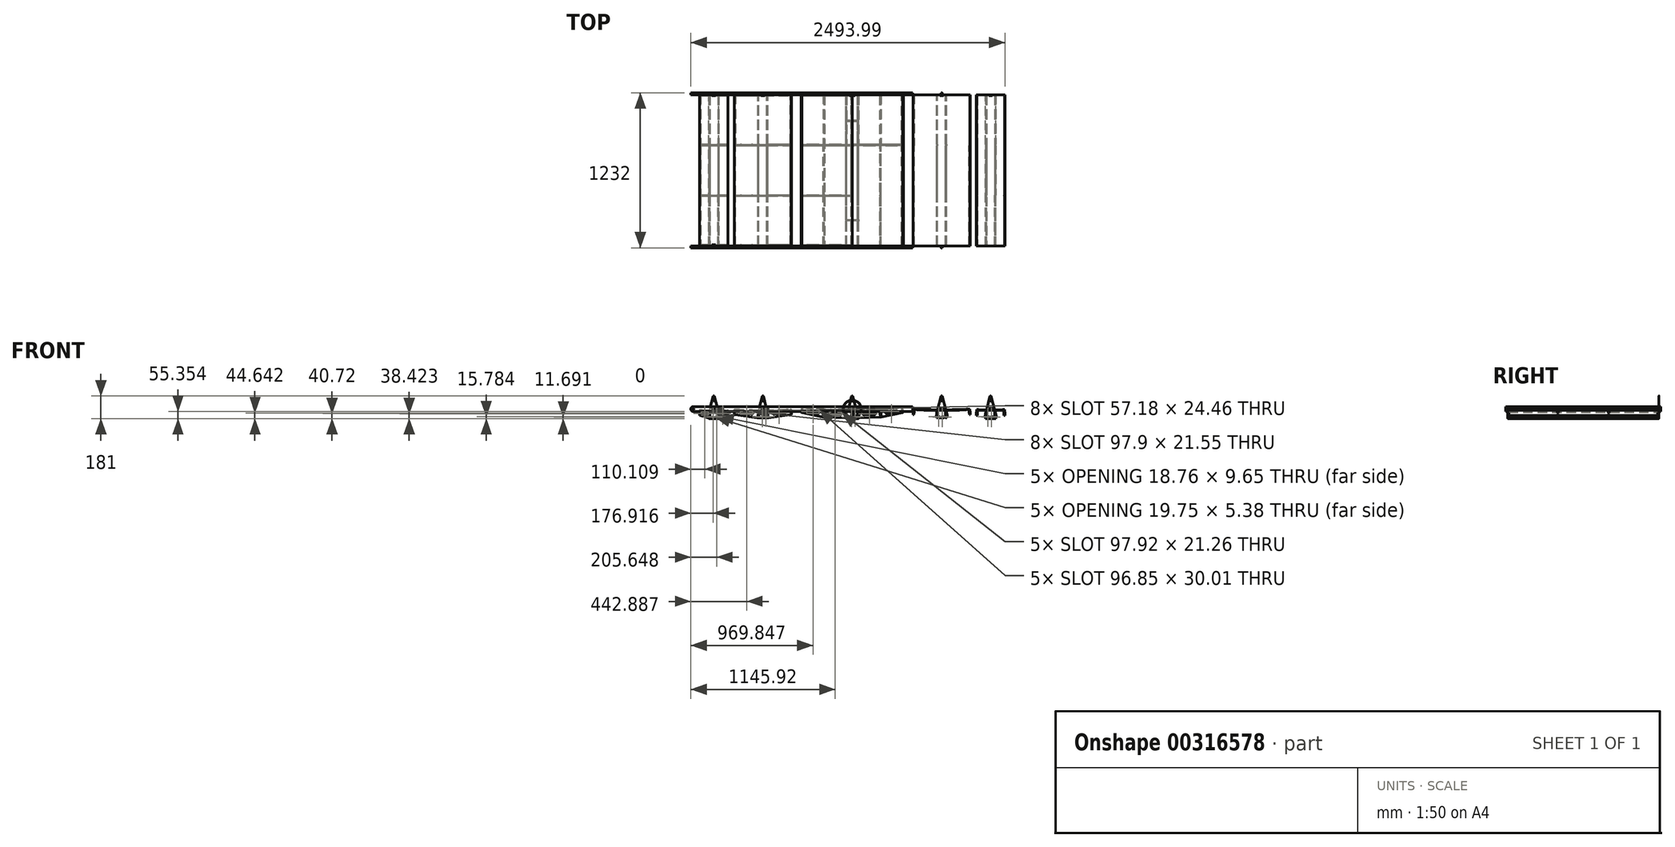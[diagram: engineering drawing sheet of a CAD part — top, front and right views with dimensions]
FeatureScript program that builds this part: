
annotation { "Feature Type Name" : "Feature", "Feature Type Description" : "" }
export const myFeature = defineFeature(function(context is Context, id is Id, definition is map)
    precondition{}
    {
        {
            assignVariable(context, id + "F0", {"name" : "ePlaque", "anyValue" : 8});
        }
        {
            assignVariable(context, id + "F1", {"name" : "lFacette", "anyValue" : 1200});
        }
        {
            var Q0;
            Q0=qCreatedBy(makeId("Front.planeOp"),FACE);
            var sketch = newSketch(context, id + "F2", { "sketchPlane" : qUnion([Q0])});
            skPoint(sketch, "E0", {"position": v(389.32, 0) * mm});
            skPoint(sketch, "E1", {"position": v(1098.97, 0) * mm});
            skPoint(sketch, "E2", {"position": v(1198.97, 1500) * mm});
            skCircle(sketch, "E3", {"center": v(0, 0) * mm, "radius": 112.5 * mm, "construction": true});
            skCircle(sketch, "E4", {"center": v(389.32, 0) * mm, "radius": 225 * mm, "construction": true});
            skCircle(sketch, "E5", {"center": v(1098.97, 0) * mm, "radius": 400 * mm, "construction": true});
            skLineSegment(sketch, "E6", {"start": v(112.5, 0) * mm, "end": v(164.32, 0) * mm, "construction": true});
            skLineSegment(sketch, "E7", {"start": v(614.32, 0) * mm, "end": v(698.97, 0) * mm, "construction": true});
            skLineSegment(sketch, "E8", {"start": v(1215.3, 382.71) * mm, "end": v(1098.97, 0) * mm, "construction": true});
            skLineSegment(sketch, "E9", {"start": v(716.26, 116.33) * mm, "end": v(1481.68, -116.33) * mm});
            skLineSegment(sketch, "E10", {"start": v(389.32, 0) * mm, "end": v(499.01, 196.45) * mm, "construction": true});
            skLineSegment(sketch, "E11", {"start": v(192.87, 109.7) * mm, "end": v(585.76, -109.7) * mm});
            skLineSegment(sketch, "E12", {"start": v(1098.97, 0) * mm, "end": v(1198.97, 1500) * mm, "construction": true});
            skLineSegment(sketch, "E13", {"start": v(389.32, 0) * mm, "end": v(1198.97, 1500) * mm, "construction": true});
            skLineSegment(sketch, "E14", {"start": v(0, 0) * mm, "end": v(1198.97, 1500) * mm, "construction": true});
            skLineSegment(sketch, "E15", {"start": v(389.32, 0) * mm, "end": v(501.82, 194.86) * mm, "construction": true});
            skLineSegment(sketch, "E16", {"start": v(0, 0) * mm, "end": v(56.25, 97.43) * mm, "construction": true});
            skLineSegment(sketch, "E17", {"start": v(1098.97, 0) * mm, "end": v(1298.97, 346.41) * mm, "construction": true});
            skLineSegment(sketch, "E18", {"start": v(-92.92, 63.43) * mm, "end": v(92.92, -63.43) * mm});
            skLineSegment(sketch, "E19", {"start": v(0, 0) * mm, "end": v(63.43, 92.92) * mm, "construction": true});
            skLineSegment(sketch, "E20", {"start": v(585.76, -109.7) * mm, "end": v(716.26, 116.33) * mm, "construction": true});
            skLineSegment(sketch, "E21", {"start": v(92.92, -63.43) * mm, "end": v(192.87, 109.7) * mm, "construction": true});
            skLineSegment(sketch, "E22", {"start": v(1198.97, 1500) * mm, "end": v(-92.92, 63.43) * mm, "construction": true});
            skSolve(sketch);
        }
        {
            var Q0;
            Q0=qCreatedBy(makeId("Front.planeOp"),FACE);
            var sketch = newSketch(context, id + "F3", { "sketchPlane" : qUnion([Q0])});
            skPoint(sketch, "E23", {"position": v(387.5, 0) * mm});
            skPoint(sketch, "E24", {"position": v(1082.5, 0) * mm});
            skPoint(sketch, "E25", {"position": v(1198.97, 1500) * mm});
            skCircle(sketch, "E26", {"center": v(0, 0) * mm, "radius": 112.5 * mm, "construction": true});
            skCircle(sketch, "E27", {"center": v(387.5, 0) * mm, "radius": 225 * mm, "construction": true});
            skCircle(sketch, "E28", {"center": v(1082.5, 0) * mm, "radius": 400 * mm, "construction": true});
            skLineSegment(sketch, "E29", {"start": v(112.5, 0) * mm, "end": v(162.5, 0) * mm, "construction": true});
            skLineSegment(sketch, "E30", {"start": v(612.5, 0) * mm, "end": v(682.5, 0) * mm, "construction": true});
            skLineSegment(sketch, "E31", {"start": v(1123.97, 1500) * mm, "end": v(1273.97, 1500) * mm});
            skLineSegment(sketch, "E32", {"start": v(1123.97, 1500) * mm, "end": v(1082.5, 0) * mm, "construction": true});
            skLineSegment(sketch, "E33", {"start": v(1273.97, 1500) * mm, "end": v(1082.5, 0) * mm, "construction": true});
            skLineSegment(sketch, "E34", {"start": v(1198.68, 1500) * mm, "end": v(1082.5, 0) * mm, "construction": true});
            skLineSegment(sketch, "E35", {"start": v(683.7, 30.89) * mm, "end": v(1481.3, -30.89) * mm});
            skLineSegment(sketch, "E36", {"start": v(1123.97, 1500) * mm, "end": v(683.7, 30.89) * mm, "construction": true});
            skLineSegment(sketch, "E37", {"start": v(1481.3, -30.89) * mm, "end": v(1273.97, 1500) * mm, "construction": true});
            skLineSegment(sketch, "E38", {"start": v(1210.93, 1636.1) * mm, "end": v(1481.3, -30.89) * mm, "construction": true});
            skLineSegment(sketch, "E39", {"start": v(683.7, 30.89) * mm, "end": v(1210.93, 1636.1) * mm, "construction": true});
            skLineSegment(sketch, "E40", {"start": v(1082.5, 0) * mm, "end": v(1210.93, 1636.1) * mm, "construction": true});
            skLineSegment(sketch, "E41", {"start": v(1210.93, 1636.1) * mm, "end": v(1337.66, 3272.32) * mm, "construction": true});
            skSolve(sketch);
        }
        {
            var Q0;
            Q0=qCreatedBy(makeId("Front.planeOp"),FACE);
            var sketch = newSketch(context, id + "F4", { "sketchPlane" : qUnion([Q0])});
            skCircle(sketch, "E42.0", {"center": v(387.5, 0) * mm, "radius": 225 * mm, "construction": true});
            skPoint(sketch, "E42.1", {"position": v(387.5, 0) * mm});
            skLineSegment(sketch, "E42.2", {"start": v(1123.97, 1500) * mm, "end": v(1273.97, 1500) * mm});
            skLineSegment(sketch, "E43", {"start": v(1123.97, 1500) * mm, "end": v(387.5, 0) * mm, "construction": true});
            skLineSegment(sketch, "E44", {"start": v(387.5, 0) * mm, "end": v(1273.97, 1500) * mm, "construction": true});
            skLineSegment(sketch, "E45", {"start": v(387.5, 0) * mm, "end": v(1197.4, 1500) * mm, "construction": true});
            skLineSegment(sketch, "E46", {"start": v(189.52, 106.9) * mm, "end": v(585.48, -106.9) * mm});
            skLineSegment(sketch, "E47", {"start": v(189.52, 106.9) * mm, "end": v(1123.97, 1500) * mm, "construction": true});
            skLineSegment(sketch, "E48", {"start": v(585.48, -106.9) * mm, "end": v(1273.97, 1500) * mm, "construction": true});
            skLineSegment(sketch, "E49", {"start": v(189.52, 106.9) * mm, "end": v(1284.6, 1650.54) * mm, "construction": true});
            skLineSegment(sketch, "E50", {"start": v(1284.6, 1650.54) * mm, "end": v(585.48, -106.9) * mm, "construction": true});
            skLineSegment(sketch, "E51", {"start": v(387.5, 0) * mm, "end": v(1284.6, 1650.54) * mm, "construction": true});
            skLineSegment(sketch, "E52", {"start": v(1284.6, 1650.54) * mm, "end": v(2181.71, 3301.09) * mm, "construction": true});
            skSolve(sketch);
        }
        {
            var Q0;
            Q0=qCreatedBy(makeId("Front.planeOp"),FACE);
            var sketch = newSketch(context, id + "F5", { "sketchPlane" : qUnion([Q0])});
            skLineSegment(sketch, "E53.0", {"start": v(1123.97, 1500) * mm, "end": v(1273.97, 1500) * mm});
            skCircle(sketch, "E54.0", {"center": v(0, 0) * mm, "radius": 112.5 * mm, "construction": true});
            skLineSegment(sketch, "E55", {"start": v(1123.97, 1500) * mm, "end": v(0, 0) * mm, "construction": true});
            skLineSegment(sketch, "E56", {"start": v(0, 0) * mm, "end": v(1273.97, 1500) * mm, "construction": true});
            skLineSegment(sketch, "E57", {"start": v(0, 0) * mm, "end": v(1197.14, 1500) * mm, "construction": true});
            skLineSegment(sketch, "E58", {"start": v(-87.93, 70.18) * mm, "end": v(87.93, -70.18) * mm});
            skLineSegment(sketch, "E59", {"start": v(-87.93, 70.18) * mm, "end": v(1123.97, 1500) * mm, "construction": true});
            skLineSegment(sketch, "E60", {"start": v(1273.97, 1500) * mm, "end": v(87.93, -70.18) * mm, "construction": true});
            skLineSegment(sketch, "E61", {"start": v(87.93, -70.18) * mm, "end": v(1294.24, 1616.9) * mm, "construction": true});
            skLineSegment(sketch, "E62", {"start": v(-87.93, 70.18) * mm, "end": v(1294.24, 1616.9) * mm, "construction": true});
            skLineSegment(sketch, "E63", {"start": v(1294.24, 1616.9) * mm, "end": v(0, 0) * mm, "construction": true});
            skLineSegment(sketch, "E64", {"start": v(1294.24, 1616.9) * mm, "end": v(2588.47, 3233.81) * mm, "construction": true});
            skSolve(sketch);
        }
        {
            var Q0;
            Q0=qCreatedBy(makeId("Front.planeOp"),FACE);
            var sketch = newSketch(context, id + "F6", { "sketchPlane" : qUnion([Q0])});
            skCircle(sketch, "E65.0", {"center": v(1098.97, 0) * mm, "radius": 400 * mm, "construction": true});
            skLineSegment(sketch, "E66.3", {"start": v(1123.97, 1500) * mm, "end": v(1273.97, 1500) * mm});
            skLineSegment(sketch, "E67", {"start": v(1337.66, 3272.32) * mm, "end": v(1098.97, 0) * mm, "construction": true});
            skLineSegment(sketch, "E68", {"start": v(751.34, -197.87) * mm, "end": v(1446.6, 197.87) * mm});
            skLineSegment(sketch, "E69", {"start": v(1446.6, 197.87) * mm, "end": v(-511.93, 2830.2) * mm, "construction": true});
            skLineSegment(sketch, "E70", {"start": v(-511.93, 2830.2) * mm, "end": v(751.34, -197.87) * mm, "construction": true});
            skLineSegment(sketch, "E71", {"start": v(52.02, 190.67) * mm, "end": v(751.34, -197.87) * mm, "construction": true});
            skLineSegment(sketch, "E72", {"start": v(747.3, 586.4) * mm, "end": v(1446.6, 197.87) * mm, "construction": true});
            skLineSegment(sketch, "E73", {"start": v(751.34, -197.87) * mm, "end": v(1190.2, 1368.3) * mm, "construction": true});
            skLineSegment(sketch, "E74", {"start": v(1190.2, 1368.3) * mm, "end": v(1446.6, 197.87) * mm, "construction": true});
            skLineSegment(sketch, "E75", {"start": v(751.34, -197.87) * mm, "end": v(1275.4, 1500) * mm, "construction": true});
            skLineSegment(sketch, "E76", {"start": v(1446.6, 197.87) * mm, "end": v(1125.4, 1500) * mm, "construction": true});
            skLineSegment(sketch, "E77", {"start": v(1125.4, 1500) * mm, "end": v(1275.4, 1500) * mm, "construction": true});
            skLineSegment(sketch, "E78", {"start": v(1198.97, 1500) * mm, "end": v(1098.97, 0) * mm, "construction": true});
            skPoint(sketch, "E79.0", {"position": v(1337.66, 3272.32) * mm});
            skSolve(sketch);
        }
        {
            var Q0;
            Q0=qCreatedBy(makeId("Front.planeOp"),FACE);
            var sketch = newSketch(context, id + "F7", { "sketchPlane" : qUnion([Q0])});
            skLineSegment(sketch, "E80", {"start": v(389.32, 0) * mm, "end": v(2181.71, 3301.09) * mm, "construction": true});
            skLineSegment(sketch, "E81", {"start": v(166.24, -29.34) * mm, "end": v(612.4, 29.34) * mm});
            skLineSegment(sketch, "E82", {"start": v(166.24, -29.34) * mm, "end": v(-99.65, 3717.55) * mm, "construction": true});
            skLineSegment(sketch, "E83", {"start": v(-99.65, 3717.55) * mm, "end": v(612.4, 29.34) * mm, "construction": true});
            skLineSegment(sketch, "E84", {"start": v(-137.98, 302.25) * mm, "end": v(166.24, -29.34) * mm, "construction": true});
            skLineSegment(sketch, "E85", {"start": v(308.18, 360.93) * mm, "end": v(612.4, 29.34) * mm, "construction": true});
            skLineSegment(sketch, "E86", {"start": v(166.24, -29.34) * mm, "end": v(1110.47, 1348.82) * mm, "construction": true});
            skLineSegment(sketch, "E87", {"start": v(1110.47, 1348.82) * mm, "end": v(612.4, 29.34) * mm, "construction": true});
            skCircle(sketch, "E88.0", {"center": v(389.32, 0) * mm, "radius": 225 * mm, "construction": true});
            skLineSegment(sketch, "E89.0", {"start": v(1123.97, 1500) * mm, "end": v(1273.97, 1500) * mm});
            skLineSegment(sketch, "E90", {"start": v(166.24, -29.34) * mm, "end": v(1273.97, 1500) * mm, "construction": true});
            skLineSegment(sketch, "E91", {"start": v(612.4, 29.34) * mm, "end": v(1123.97, 1500) * mm, "construction": true});
            skPoint(sketch, "E92.0", {"position": v(2181.71, 3301.09) * mm});
            skSolve(sketch);
        }
        {
            var Q0;
            Q0=qCreatedBy(makeId("Front.planeOp"),FACE);
            var sketch = newSketch(context, id + "F8", { "sketchPlane" : qUnion([Q0])});
            skLineSegment(sketch, "E93", {"start": v(0, 0) * mm, "end": v(2588.47, 3233.81) * mm, "construction": true});
            skLineSegment(sketch, "E94", {"start": v(-111.64, 13.9) * mm, "end": v(111.64, -13.9) * mm});
            skLineSegment(sketch, "E95", {"start": v(-111.64, 13.9) * mm, "end": v(511.32, 4108.97) * mm, "construction": true});
            skLineSegment(sketch, "E96", {"start": v(-203.86, 219.13) * mm, "end": v(-111.64, 13.9) * mm, "construction": true});
            skLineSegment(sketch, "E97", {"start": v(511.32, 4108.97) * mm, "end": v(111.64, -13.9) * mm, "construction": true});
            skLineSegment(sketch, "E98", {"start": v(19.42, 191.34) * mm, "end": v(111.64, -13.9) * mm, "construction": true});
            skLineSegment(sketch, "E99", {"start": v(111.64, -13.9) * mm, "end": v(1100.2, 1383.84) * mm, "construction": true});
            skLineSegment(sketch, "E100", {"start": v(-111.64, 13.9) * mm, "end": v(1100.2, 1383.84) * mm, "construction": true});
            skLineSegment(sketch, "E101.0", {"start": v(1123.97, 1500) * mm, "end": v(1273.97, 1500) * mm});
            skCircle(sketch, "E102.0", {"center": v(0, 0) * mm, "radius": 112.5 * mm, "construction": true});
            skPoint(sketch, "E103.0", {"position": v(2588.47, 3233.81) * mm});
            skLineSegment(sketch, "E104", {"start": v(111.64, -13.9) * mm, "end": v(1123.97, 1500) * mm, "construction": true});
            skLineSegment(sketch, "E105", {"start": v(-111.64, 13.9) * mm, "end": v(1273.97, 1500) * mm, "construction": true});
            skSolve(sketch);
        }
        {
            var Q0;
            Q0=qCreatedBy(makeId("Front.planeOp"),FACE);
            var sketch = newSketch(context, id + "F9", { "sketchPlane" : qUnion([Q0])});
            skArc(sketch, "E106", {"start": v(-112.5, -9.47) * mm, "mid": v(0, -11) * mm, "end": v(112.5, -9.47) * mm});
            skLineSegment(sketch, "E107", {"start": v(-13.5, -5.98) * mm, "end": v(-13.5, 6) * mm});
            skLineSegment(sketch, "E108", {"start": v(-13.5, 6) * mm, "end": v(13.5, 6) * mm});
            skLineSegment(sketch, "E109", {"start": v(13.5, 6) * mm, "end": v(13.5, 0.5) * mm});
            skLineSegment(sketch, "E110", {"start": v(0, 0) * mm, "end": v(0, -6) * mm, "construction": true});
            skArc(sketch, "E111", {"start": v(4.47, 0.5) * mm, "mid": v(-4.5, 0) * mm, "end": v(4.47, -0.5) * mm});
            skLineSegment(sketch, "E112", {"start": v(-35.49, -10.85) * mm, "end": v(-36, -70.85) * mm, "construction": true});
            skLineSegment(sketch, "E113", {"start": v(-40, -70.81) * mm, "end": v(-32, -70.88) * mm});
            skLineSegment(sketch, "E114", {"start": v(-40, -70.81) * mm, "end": v(-39.49, -10.81) * mm});
            skLineSegment(sketch, "E115", {"start": v(-32, -70.88) * mm, "end": v(-31.49, -10.88) * mm});
            skLineSegment(sketch, "E116", {"start": v(-108.5, -9.58) * mm, "end": v(-109.55, -49.57) * mm, "construction": true});
            skLineSegment(sketch, "E117", {"start": v(-112.5, -9.47) * mm, "end": v(-113.55, -49.46) * mm});
            skLineSegment(sketch, "E118", {"start": v(-113.55, -49.46) * mm, "end": v(-105.55, -49.67) * mm});
            skLineSegment(sketch, "E119", {"start": v(-105.55, -49.67) * mm, "end": v(-104.5, -9.68) * mm});
            skArc(sketch, "E120", {"start": v(-112.36, -4.48) * mm, "mid": v(0, -6) * mm, "end": v(112.36, -4.48) * mm});
            skLineSegment(sketch, "E121", {"start": v(-112.36, -4.48) * mm, "end": v(-112.5, -9.47) * mm});
            skLineSegment(sketch, "E122", {"start": v(112.5, -9.47) * mm, "end": v(112.36, -4.48) * mm});
            skLineSegment(sketch, "E123.MirrorCS", {"start": v(113.55, -49.46) * mm, "end": v(105.55, -49.67) * mm});
            skLineSegment(sketch, "E124.MirrorCS", {"start": v(112.5, -9.47) * mm, "end": v(113.55, -49.46) * mm});
            skLineSegment(sketch, "E125.MirrorCS", {"start": v(105.55, -49.67) * mm, "end": v(104.5, -9.68) * mm});
            skLineSegment(sketch, "E126.MirrorCS", {"start": v(40, -70.81) * mm, "end": v(39.49, -10.81) * mm});
            skLineSegment(sketch, "E127.MirrorCS", {"start": v(32, -70.88) * mm, "end": v(31.49, -10.88) * mm});
            skLineSegment(sketch, "E128.MirrorCS", {"start": v(40, -70.81) * mm, "end": v(32, -70.88) * mm});
            skLineSegment(sketch, "E129.bottom", {"start": v(-40, -70.81) * mm, "end": v(40, -70.81) * mm, "construction": true});
            skLineSegment(sketch, "E129.left", {"start": v(-40, -70.81) * mm, "end": v(-40, -75.81) * mm});
            skLineSegment(sketch, "E129.right", {"start": v(40, -70.81) * mm, "end": v(40, -75.81) * mm});
            skLineSegment(sketch, "E130", {"start": v(-105.55, -49.67) * mm, "end": v(-40, -70.81) * mm});
            skLineSegment(sketch, "E131", {"start": v(-113.02, -29.47) * mm, "end": v(-105.03, -29.68) * mm});
            skLineSegment(sketch, "E132", {"start": v(-39.74, -40.81) * mm, "end": v(-31.74, -40.88) * mm});
            skLineSegment(sketch, "E133.MirrorCS", {"start": v(113.02, -29.47) * mm, "end": v(105.03, -29.68) * mm});
            skLineSegment(sketch, "E134.MirrorCS", {"start": v(105.55, -49.67) * mm, "end": v(40, -70.81) * mm});
            skLineSegment(sketch, "E135.MirrorCS", {"start": v(39.74, -40.81) * mm, "end": v(31.74, -40.88) * mm});
            skArc(sketch, "E136", {"start": v(393.79, 0.5) * mm, "mid": v(384.82, 0) * mm, "end": v(393.79, -0.5) * mm});
            skLineSegment(sketch, "E137", {"start": v(389.32, 0) * mm, "end": v(389.32, -6) * mm, "construction": true});
            skArc(sketch, "E138", {"start": v(164.32, 0.74) * mm, "mid": v(389.32, -6) * mm, "end": v(614.32, 0.74) * mm});
            skArc(sketch, "E139", {"start": v(164.02, -4.25) * mm, "mid": v(389.32, -11) * mm, "end": v(614.62, -4.25) * mm});
            skLineSegment(sketch, "E140", {"start": v(164.32, 0.74) * mm, "end": v(164.02, -4.25) * mm});
            skLineSegment(sketch, "E141", {"start": v(353.32, -70.83) * mm, "end": v(353.88, -10.83) * mm, "construction": true});
            skLineSegment(sketch, "E142", {"start": v(165.66, -44.41) * mm, "end": v(168, -4.48) * mm, "construction": true});
            skLineSegment(sketch, "E143", {"start": v(164.02, -4.25) * mm, "end": v(161.66, -44.18) * mm});
            skLineSegment(sketch, "E144", {"start": v(161.66, -44.18) * mm, "end": v(169.65, -44.65) * mm});
            skLineSegment(sketch, "E145", {"start": v(169.65, -44.65) * mm, "end": v(172, -4.72) * mm});
            skLineSegment(sketch, "E146", {"start": v(349.88, -10.8) * mm, "end": v(349.32, -70.8) * mm});
            skLineSegment(sketch, "E147", {"start": v(349.32, -70.8) * mm, "end": v(357.32, -70.87) * mm});
            skLineSegment(sketch, "E148", {"start": v(357.32, -70.87) * mm, "end": v(357.88, -10.87) * mm});
            skLineSegment(sketch, "E149.MirrorCS", {"start": v(421.32, -70.87) * mm, "end": v(420.75, -10.87) * mm});
            skLineSegment(sketch, "E150.MirrorCS", {"start": v(428.75, -10.8) * mm, "end": v(429.32, -70.8) * mm});
            skLineSegment(sketch, "E151.MirrorCS", {"start": v(429.32, -70.8) * mm, "end": v(421.32, -70.87) * mm});
            skLineSegment(sketch, "E152.MirrorCS", {"start": v(614.62, -4.25) * mm, "end": v(616.97, -44.18) * mm});
            skLineSegment(sketch, "E153.MirrorCS", {"start": v(616.97, -44.18) * mm, "end": v(608.98, -44.65) * mm});
            skLineSegment(sketch, "E154.MirrorCS", {"start": v(608.98, -44.65) * mm, "end": v(606.63, -4.72) * mm});
            skLineSegment(sketch, "E155.bottom", {"start": v(349.32, -70.8) * mm, "end": v(429.32, -70.8) * mm, "construction": true});
            skLineSegment(sketch, "E156", {"start": v(169.65, -44.65) * mm, "end": v(349.32, -70.8) * mm});
            skLineSegment(sketch, "E157", {"start": v(162.84, -24.21) * mm, "end": v(170.83, -24.68) * mm});
            skLineSegment(sketch, "E158", {"start": v(349.6, -40.8) * mm, "end": v(357.6, -40.87) * mm});
            skLineSegment(sketch, "E159.MirrorCS", {"start": v(429.03, -40.8) * mm, "end": v(421.03, -40.87) * mm});
            skLineSegment(sketch, "E160.MirrorCS", {"start": v(608.98, -44.65) * mm, "end": v(429.32, -70.8) * mm});
            skLineSegment(sketch, "E161.MirrorCS", {"start": v(615.8, -24.21) * mm, "end": v(607.8, -24.68) * mm});
            skLineSegment(sketch, "E162.MirrorCS", {"start": v(614.32, 0.74) * mm, "end": v(614.62, -4.25) * mm});
            skLineSegment(sketch, "E163", {"start": v(375.82, -5.98) * mm, "end": v(375.82, 6) * mm});
            skLineSegment(sketch, "E164", {"start": v(375.82, 6) * mm, "end": v(402.82, 6) * mm});
            skLineSegment(sketch, "E165", {"start": v(402.82, 6) * mm, "end": v(402.82, 0.5) * mm});
            skLineSegment(sketch, "E166", {"start": v(0, 0) * mm, "end": v(13.5, 0) * mm, "construction": true});
            skLineSegment(sketch, "E167", {"start": v(13.5, 0.5) * mm, "end": v(4.47, 0.5) * mm});
            skLineSegment(sketch, "E168", {"start": v(13.5, -0.5) * mm, "end": v(4.47, -0.5) * mm});
            skLineSegment(sketch, "E169.trimOffspring", {"start": v(13.5, -0.5) * mm, "end": v(13.5, -5.98) * mm});
            skLineSegment(sketch, "E170", {"start": v(13.5, 0.5) * mm, "end": v(13.5, -0.5) * mm, "construction": true});
            skLineSegment(sketch, "E171", {"start": v(402.82, 0.5) * mm, "end": v(393.79, 0.5) * mm});
            skLineSegment(sketch, "E172", {"start": v(402.82, -0.5) * mm, "end": v(393.79, -0.5) * mm});
            skLineSegment(sketch, "E173.trimOffspring", {"start": v(402.82, -0.5) * mm, "end": v(402.82, -5.98) * mm});
            skPoint(sketch, "E174", {"position": v(1098.97, 0) * mm});
            skCircle(sketch, "E175", {"center": v(1098.97, 0) * mm, "radius": 4.5 * mm});
            skArc(sketch, "E176", {"start": v(698.97, 18.45) * mm, "mid": v(1098.97, -6) * mm, "end": v(1498.97, 18.45) * mm});
            skLineSegment(sketch, "E177", {"start": v(1098.97, 0) * mm, "end": v(1098.97, -6) * mm, "construction": true});
            skLineSegment(sketch, "E178", {"start": v(698.97, 18.45) * mm, "end": v(698.36, 13.49) * mm});
            skLineSegment(sketch, "E179.MirrorCS", {"start": v(1498.97, 18.45) * mm, "end": v(1499.58, 13.49) * mm});
            skArc(sketch, "E180", {"start": v(698.36, 13.49) * mm, "mid": v(1098.97, -11) * mm, "end": v(1499.58, 13.49) * mm});
            skLineSegment(sketch, "E181", {"start": v(702.33, 13) * mm, "end": v(697.5, -26.7) * mm, "construction": true});
            skLineSegment(sketch, "E182", {"start": v(706.3, 12.52) * mm, "end": v(701.48, -27.19) * mm});
            skLineSegment(sketch, "E183", {"start": v(701.48, -27.19) * mm, "end": v(693.54, -26.22) * mm});
            skLineSegment(sketch, "E184", {"start": v(693.54, -26.22) * mm, "end": v(698.36, 13.49) * mm});
            skLineSegment(sketch, "E185", {"start": v(695.95, -6.37) * mm, "end": v(703.9, -7.33) * mm});
            skLineSegment(sketch, "E186.MirrorCS", {"start": v(1496.46, -27.19) * mm, "end": v(1504.4, -26.22) * mm});
            skLineSegment(sketch, "E187.MirrorCS", {"start": v(1504.4, -26.22) * mm, "end": v(1499.58, 13.49) * mm});
            skLineSegment(sketch, "E188.MirrorCS", {"start": v(1491.64, 12.52) * mm, "end": v(1496.46, -27.19) * mm});
            skLineSegment(sketch, "E189.MirrorCS", {"start": v(1502, -6.37) * mm, "end": v(1494.05, -7.33) * mm});
            skLineSegment(sketch, "E190", {"start": v(876.94, -3.5) * mm, "end": v(872.9, -63.36) * mm, "construction": true});
            skLineSegment(sketch, "E191", {"start": v(872.95, -3.23) * mm, "end": v(868.9, -63.1) * mm});
            skLineSegment(sketch, "E192", {"start": v(868.9, -63.1) * mm, "end": v(876.88, -63.63) * mm});
            skLineSegment(sketch, "E193", {"start": v(876.88, -63.63) * mm, "end": v(880.93, -3.77) * mm});
            skLineSegment(sketch, "E194", {"start": v(870.93, -33.16) * mm, "end": v(878.9, -33.7) * mm});
            skLineSegment(sketch, "E195", {"start": v(701.48, -27.19) * mm, "end": v(868.9, -63.1) * mm});
            skLineSegment(sketch, "E196", {"start": v(1098.97, -11) * mm, "end": v(1098.97, -51) * mm});
            skLineSegment(sketch, "E197", {"start": v(1090.97, -11) * mm, "end": v(1090.97, -51) * mm});
            skLineSegment(sketch, "E198", {"start": v(1090.97, -51) * mm, "end": v(1106.97, -51) * mm});
            skLineSegment(sketch, "E199", {"start": v(1106.97, -51) * mm, "end": v(1106.97, -11) * mm});
            skLineSegment(sketch, "E200", {"start": v(1090.97, -31) * mm, "end": v(1098.97, -31) * mm});
            skLineSegment(sketch, "E201", {"start": v(1098.97, -31) * mm, "end": v(1106.97, -31) * mm});
            skLineSegment(sketch, "E202.bottom", {"start": v(1047.97, -75.66) * mm, "end": v(1149.97, -75.66) * mm});
            skLineSegment(sketch, "E202.top", {"start": v(1047.97, -70.66) * mm, "end": v(1149.97, -70.66) * mm});
            skLineSegment(sketch, "E202.left", {"start": v(1047.97, -75.66) * mm, "end": v(1047.97, -70.66) * mm});
            skLineSegment(sketch, "E202.right", {"start": v(1149.97, -75.66) * mm, "end": v(1149.97, -70.66) * mm});
            skLineSegment(sketch, "E203", {"start": v(1047.97, -70.66) * mm, "end": v(1047.97, -10.66) * mm});
            skLineSegment(sketch, "E204", {"start": v(1047.97, -10.66) * mm, "end": v(1055.97, -10.66) * mm});
            skLineSegment(sketch, "E205", {"start": v(1055.97, -10.66) * mm, "end": v(1055.97, -70.66) * mm});
            skLineSegment(sketch, "E206", {"start": v(1047.97, -40.66) * mm, "end": v(1055.97, -40.66) * mm});
            skLineSegment(sketch, "E207.MirrorCS", {"start": v(1149.97, -70.66) * mm, "end": v(1149.97, -10.66) * mm});
            skLineSegment(sketch, "E208.MirrorCS", {"start": v(1149.97, -10.66) * mm, "end": v(1141.97, -10.66) * mm});
            skLineSegment(sketch, "E209.MirrorCS", {"start": v(1141.97, -10.66) * mm, "end": v(1141.97, -70.66) * mm});
            skLineSegment(sketch, "E210.MirrorCS", {"start": v(1149.97, -40.66) * mm, "end": v(1141.97, -40.66) * mm});
            skLineSegment(sketch, "E211", {"start": v(876.88, -63.63) * mm, "end": v(1047.97, -70.66) * mm});
            skLineSegment(sketch, "E212.MirrorCS", {"start": v(1496.46, -27.19) * mm, "end": v(1329.04, -63.1) * mm});
            skLineSegment(sketch, "E213.MirrorCS", {"start": v(1321.06, -63.63) * mm, "end": v(1149.97, -70.66) * mm});
            skLineSegment(sketch, "E214.MirrorCS", {"start": v(1329.04, -63.1) * mm, "end": v(1321.06, -63.63) * mm});
            skLineSegment(sketch, "E215.MirrorCS", {"start": v(1324.99, -3.23) * mm, "end": v(1329.04, -63.1) * mm});
            skLineSegment(sketch, "E216.MirrorCS", {"start": v(1321.06, -63.63) * mm, "end": v(1317, -3.77) * mm});
            skLineSegment(sketch, "E217.MirrorCS", {"start": v(1327.01, -33.16) * mm, "end": v(1319.03, -33.7) * mm});
            skLineSegment(sketch, "E218", {"start": v(1098.97, -6) * mm, "end": v(1098.97, -11) * mm});
            skLineSegment(sketch, "E219", {"start": v(1051.97, -10.66) * mm, "end": v(1051.97, -40.66) * mm, "construction": true});
            skArc(sketch, "E220", {"start": v(-40, -70.81) * mm, "mid": v(0, -71) * mm, "end": v(40, -70.81) * mm});
            skArc(sketch, "E221", {"start": v(-40, -75.81) * mm, "mid": v(0, -76) * mm, "end": v(40, -75.81) * mm});
            skArc(sketch, "E222", {"start": v(349.32, -70.8) * mm, "mid": v(389.32, -71) * mm, "end": v(429.32, -70.8) * mm});
            skLineSegment(sketch, "E223", {"start": v(1047.97, -73.16) * mm, "end": v(1098.97, -73.16) * mm, "construction": true});
            skLineSegment(sketch, "E224", {"start": v(1098.97, 0) * mm, "end": v(1098.97, -51) * mm, "construction": true});
            skLineSegment(sketch, "E225", {"start": v(1098.97, -51) * mm, "end": v(1098.97, -70.66) * mm});
            skLineSegment(sketch, "E226", {"start": v(1090.97, -51) * mm, "end": v(1083.97, -51) * mm});
            skLineSegment(sketch, "E227", {"start": v(1083.97, -51) * mm, "end": v(1083.97, -59) * mm});
            skLineSegment(sketch, "E228.MirrorCS", {"start": v(1106.97, -51) * mm, "end": v(1113.97, -51) * mm});
            skLineSegment(sketch, "E229.MirrorCS", {"start": v(1113.97, -51) * mm, "end": v(1113.97, -59) * mm});
            skLineSegment(sketch, "E230", {"start": v(1083.97, -59) * mm, "end": v(1113.97, -59) * mm});
            skLineSegment(sketch, "E231", {"start": v(1083.97, -55) * mm, "end": v(1098.97, -55) * mm, "construction": true});
            skLineSegment(sketch, "E232", {"start": v(1051.97, -70.66) * mm, "end": v(1051.97, -55.66) * mm, "construction": true});
            skLineSegment(sketch, "E233", {"start": v(1047.97, -63.16) * mm, "end": v(1055.97, -63.16) * mm});
            skLineSegment(sketch, "E234", {"start": v(1098.97, -63.16) * mm, "end": v(1051.97, -63.16) * mm, "construction": true});
            skLineSegment(sketch, "E235", {"start": v(1055.97, -55.66) * mm, "end": v(1141.97, -55) * mm});
            skLineSegment(sketch, "E236.MirrorCS", {"start": v(1149.97, -63.16) * mm, "end": v(1141.97, -63.16) * mm});
            skLineSegment(sketch, "E237", {"start": v(1076.44, -5.92) * mm, "end": v(1076.44, -0.5) * mm});
            skLineSegment(sketch, "E238", {"start": v(1076.44, -0.5) * mm, "end": v(1094.5, -0.5) * mm});
            skLineSegment(sketch, "E239.bottom", {"start": v(1085.47, 6) * mm, "end": v(1112.47, 6) * mm});
            skLineSegment(sketch, "E239.top", {"start": v(1085.47, 0.5) * mm, "end": v(1112.47, 0.5) * mm});
            skLineSegment(sketch, "E239.left", {"start": v(1085.47, 6) * mm, "end": v(1085.47, 0.5) * mm});
            skLineSegment(sketch, "E239.right", {"start": v(1112.47, 6) * mm, "end": v(1112.47, 0.5) * mm});
            skCircle(sketch, "E240", {"center": v(1098.97, 0) * mm, "radius": 6 * mm});
            skLineSegment(sketch, "E241.MirrorCS", {"start": v(1121.5, -0.5) * mm, "end": v(1103.44, -0.5) * mm});
            skLineSegment(sketch, "E242.MirrorCS", {"start": v(1121.5, -5.92) * mm, "end": v(1121.5, -0.5) * mm});
            skLineSegment(sketch, "E243", {"start": v(1085.47, 0.5) * mm, "end": v(1076.44, 0.5) * mm, "construction": true});
            skCircle(sketch, "E244", {"center": v(0, 0) * mm, "radius": 3 * mm});
            skPoint(sketch, "E245.0", {"position": v(1337.66, 3272.32) * mm});
            skPoint(sketch, "E246.0", {"position": v(2181.71, 3301.09) * mm});
            skPoint(sketch, "E247.0", {"position": v(2588.47, 3233.81) * mm});
            skLineSegment(sketch, "E248", {"start": v(1337.66, 3272.32) * mm, "end": v(1098.97, 0) * mm, "construction": true});
            skLineSegment(sketch, "E249", {"start": v(1098.97, -3) * mm, "end": v(1098.97, 3278.02) * mm, "construction": true});
            skLineSegment(sketch, "E250", {"start": v(389.32, 0) * mm, "end": v(2181.71, 3301.09) * mm, "construction": true});
            skLineSegment(sketch, "E251", {"start": v(389.32, -6) * mm, "end": v(389.32, 3750.31) * mm, "construction": true});
            skLineSegment(sketch, "E252", {"start": v(0, 0) * mm, "end": v(2588.47, 3233.81) * mm, "construction": true});
            skLineSegment(sketch, "E253", {"start": v(0, -6) * mm, "end": v(0, 4136.19) * mm, "construction": true});
            skLineSegment(sketch, "E254", {"start": v(349.32, -70.8) * mm, "end": v(349.32, -75.8) * mm});
            skSolve(sketch);
        }
        {
            var Q0;
            Q0=qCreatedBy(makeId("Front.planeOp"),FACE);
            var sketch = newSketch(context, id + "F10", { "sketchPlane" : qUnion([Q0])});
            skArc(sketch, "E255.0", {"start": v(-104.5, -9.68) * mm, "mid": v(0, -11) * mm, "end": v(104.5, -9.68) * mm});
            skLineSegment(sketch, "E255.2", {"start": v(-113.02, -29.47) * mm, "end": v(-105.03, -29.68) * mm});
            skLineSegment(sketch, "E255.5", {"start": v(-39.95, -65.37) * mm, "end": v(-39.74, -40.81) * mm});
            skLineSegment(sketch, "E255.6", {"start": v(-39.74, -40.81) * mm, "end": v(-31.74, -40.88) * mm});
            skLineSegment(sketch, "E255.7", {"start": v(-31.97, -66.87) * mm, "end": v(-31.74, -40.88) * mm});
            skLineSegment(sketch, "E255.9", {"start": v(31.97, -66.87) * mm, "end": v(31.74, -40.88) * mm});
            skLineSegment(sketch, "E255.10", {"start": v(39.74, -40.81) * mm, "end": v(31.74, -40.88) * mm});
            skLineSegment(sketch, "E255.11", {"start": v(39.95, -65.37) * mm, "end": v(39.74, -40.81) * mm});
            skLineSegment(sketch, "E255.12", {"start": v(105.55, -49.67) * mm, "end": v(45.18, -69.14) * mm});
            skLineSegment(sketch, "E255.14", {"start": v(113.02, -29.47) * mm, "end": v(105.03, -29.68) * mm});
            skArc(sketch, "E255.16", {"start": v(172, -4.72) * mm, "mid": v(389.32, -11) * mm, "end": v(606.63, -4.72) * mm});
            skLineSegment(sketch, "E255.19", {"start": v(162.84, -24.21) * mm, "end": v(170.83, -24.68) * mm});
            skLineSegment(sketch, "E255.22", {"start": v(357.35, -66.86) * mm, "end": v(357.6, -40.87) * mm});
            skLineSegment(sketch, "E255.23", {"start": v(349.6, -40.8) * mm, "end": v(349.36, -66.21) * mm});
            skLineSegment(sketch, "E255.24", {"start": v(349.6, -40.8) * mm, "end": v(357.6, -40.87) * mm});
            skLineSegment(sketch, "E255.25", {"start": v(429.03, -40.8) * mm, "end": v(421.03, -40.87) * mm});
            skLineSegment(sketch, "E255.26", {"start": v(421.28, -66.86) * mm, "end": v(421.03, -40.87) * mm});
            skLineSegment(sketch, "E255.27", {"start": v(429.03, -40.8) * mm, "end": v(429.27, -66.21) * mm});
            skLineSegment(sketch, "E255.28", {"start": v(608.98, -44.65) * mm, "end": v(433.85, -70.13) * mm});
            skLineSegment(sketch, "E255.30", {"start": v(615.8, -24.21) * mm, "end": v(607.8, -24.68) * mm});
            skLineSegment(sketch, "E256.0", {"start": v(0, 0) * mm, "end": v(0, -6) * mm, "construction": true});
            skLineSegment(sketch, "E256.1", {"start": v(389.32, 0) * mm, "end": v(389.32, -6) * mm, "construction": true});
            skLineSegment(sketch, "E257.0", {"start": v(-105.55, -49.67) * mm, "end": v(-45.18, -69.14) * mm});
            skLineSegment(sketch, "E258", {"start": v(-91.62, -9.99) * mm, "end": v(-92.6, -53.85) * mm, "construction": true});
            skLineSegment(sketch, "E259", {"start": v(-52.32, -10.67) * mm, "end": v(-53.03, -66.61) * mm, "construction": true});
            skLineSegment(sketch, "E260", {"start": v(-92.1, -31.92) * mm, "end": v(-52.67, -38.64) * mm, "construction": true});
            skArc(sketch, "E261", {"start": v(-93.62, -40.8) * mm, "mid": v(-100.98, -30.4) * mm, "end": v(-90.6, -23.05) * mm});
            skArc(sketch, "E262", {"start": v(-54.19, -47.51) * mm, "mid": v(-43.8, -40.15) * mm, "end": v(-51.16, -29.77) * mm});
            skLineSegment(sketch, "E263", {"start": v(-93.62, -40.8) * mm, "end": v(-54.19, -47.51) * mm});
            skLineSegment(sketch, "E264", {"start": v(-51.16, -29.77) * mm, "end": v(-90.6, -23.05) * mm});
            skLineSegment(sketch, "E265", {"start": v(-105.03, -29.68) * mm, "end": v(-92.1, -31.92) * mm, "construction": true});
            skLineSegment(sketch, "E266", {"start": v(-52.67, -38.64) * mm, "end": v(-39.74, -40.81) * mm, "construction": true});
            skLineSegment(sketch, "E267.MirrorCS", {"start": v(51.16, -29.77) * mm, "end": v(90.6, -23.05) * mm});
            skArc(sketch, "E268.MirrorCS", {"start": v(54.19, -47.51) * mm, "mid": v(43.8, -40.15) * mm, "end": v(51.16, -29.77) * mm});
            skLineSegment(sketch, "E269.MirrorCS", {"start": v(93.62, -40.8) * mm, "end": v(54.19, -47.51) * mm});
            skArc(sketch, "E270.MirrorCS", {"start": v(93.62, -40.8) * mm, "mid": v(100.98, -30.4) * mm, "end": v(90.6, -23.05) * mm});
            skLineSegment(sketch, "E271.0", {"start": v(169.65, -44.65) * mm, "end": v(344.78, -70.13) * mm});
            skLineSegment(sketch, "E272", {"start": v(221.42, -7.25) * mm, "end": v(219.43, -51.9) * mm, "construction": true});
            skLineSegment(sketch, "E273", {"start": v(300.9, -9.96) * mm, "end": v(299.63, -63.56) * mm, "construction": true});
            skLineSegment(sketch, "E274", {"start": v(220.43, -29.57) * mm, "end": v(300.35, -33.14) * mm, "construction": true});
            skLineSegment(sketch, "E275", {"start": v(300.35, -33.14) * mm, "end": v(349.6, -40.8) * mm, "construction": true});
            skLineSegment(sketch, "E276", {"start": v(170.83, -24.68) * mm, "end": v(220.43, -29.57) * mm, "construction": true});
            skArc(sketch, "E277", {"start": v(220.03, -38.56) * mm, "mid": v(211.44, -29.17) * mm, "end": v(220.83, -20.58) * mm});
            skArc(sketch, "E278", {"start": v(299.95, -42.13) * mm, "mid": v(309.34, -33.54) * mm, "end": v(300.75, -24.15) * mm});
            skLineSegment(sketch, "E279", {"start": v(220.83, -20.58) * mm, "end": v(300.75, -24.15) * mm});
            skLineSegment(sketch, "E280", {"start": v(220.03, -38.56) * mm, "end": v(299.95, -42.13) * mm});
            skLineSegment(sketch, "E281.MirrorCS", {"start": v(557.8, -20.58) * mm, "end": v(477.88, -24.15) * mm});
            skArc(sketch, "E282.MirrorCS", {"start": v(478.69, -42.13) * mm, "mid": v(469.3, -33.54) * mm, "end": v(477.88, -24.15) * mm});
            skLineSegment(sketch, "E283.MirrorCS", {"start": v(558.6, -38.56) * mm, "end": v(478.69, -42.13) * mm});
            skArc(sketch, "E284.MirrorCS", {"start": v(558.6, -38.56) * mm, "mid": v(567.2, -29.17) * mm, "end": v(557.8, -20.58) * mm});
            skLineSegment(sketch, "E285.0", {"start": v(-105.03, -29.68) * mm, "end": v(-104.5, -9.68) * mm});
            skLineSegment(sketch, "E285.1", {"start": v(-113.02, -29.47) * mm, "end": v(-113.55, -49.46) * mm});
            skLineSegment(sketch, "E285.2", {"start": v(-113.55, -49.46) * mm, "end": v(-105.55, -49.67) * mm});
            skLineSegment(sketch, "E286.MirrorCS", {"start": v(105.03, -29.68) * mm, "end": v(104.5, -9.68) * mm});
            skLineSegment(sketch, "E287.MirrorCS", {"start": v(113.02, -29.47) * mm, "end": v(113.55, -49.46) * mm});
            skLineSegment(sketch, "E288.MirrorCS", {"start": v(113.55, -49.46) * mm, "end": v(105.55, -49.67) * mm});
            skLineSegment(sketch, "E289.0", {"start": v(170.83, -24.68) * mm, "end": v(172, -4.72) * mm});
            skLineSegment(sketch, "E289.1", {"start": v(162.84, -24.21) * mm, "end": v(161.66, -44.18) * mm});
            skLineSegment(sketch, "E289.2", {"start": v(161.66, -44.18) * mm, "end": v(169.65, -44.65) * mm});
            skLineSegment(sketch, "E290.MirrorCS", {"start": v(607.8, -24.68) * mm, "end": v(606.63, -4.72) * mm});
            skLineSegment(sketch, "E291.MirrorCS", {"start": v(615.8, -24.21) * mm, "end": v(616.97, -44.18) * mm});
            skLineSegment(sketch, "E292.MirrorCS", {"start": v(616.97, -44.18) * mm, "end": v(608.98, -44.65) * mm});
            skLineSegment(sketch, "E293.0", {"start": v(1098.97, 0) * mm, "end": v(1098.97, -6) * mm, "construction": true});
            skArc(sketch, "E294.0", {"start": v(706.3, 12.52) * mm, "mid": v(898.3, -4.87) * mm, "end": v(1090.97, -11) * mm});
            skLineSegment(sketch, "E294.1", {"start": v(701.48, -27.19) * mm, "end": v(864.38, -62.12) * mm});
            skLineSegment(sketch, "E294.2", {"start": v(693.54, -26.22) * mm, "end": v(695.95, -6.37) * mm});
            skLineSegment(sketch, "E294.3", {"start": v(701.48, -27.19) * mm, "end": v(693.54, -26.22) * mm});
            skLineSegment(sketch, "E294.4", {"start": v(695.95, -6.37) * mm, "end": v(703.9, -7.33) * mm});
            skLineSegment(sketch, "E294.5", {"start": v(706.3, 12.52) * mm, "end": v(703.9, -7.33) * mm});
            skLineSegment(sketch, "E294.6", {"start": v(870.93, -33.16) * mm, "end": v(869.21, -58.48) * mm});
            skLineSegment(sketch, "E294.7", {"start": v(877.16, -59.53) * mm, "end": v(878.9, -33.7) * mm});
            skLineSegment(sketch, "E294.8", {"start": v(870.93, -33.16) * mm, "end": v(878.9, -33.7) * mm});
            skLineSegment(sketch, "E294.9", {"start": v(880.99, -63.8) * mm, "end": v(1043.8, -70.5) * mm});
            skLineSegment(sketch, "E294.10", {"start": v(1047.97, -66.5) * mm, "end": v(1047.97, -40.66) * mm});
            skLineSegment(sketch, "E294.11", {"start": v(1047.97, -40.66) * mm, "end": v(1055.97, -40.66) * mm});
            skLineSegment(sketch, "E294.12", {"start": v(1055.97, -40.66) * mm, "end": v(1055.97, -66.66) * mm});
            skLineSegment(sketch, "E294.14", {"start": v(1090.97, -31) * mm, "end": v(1098.97, -31) * mm});
            skLineSegment(sketch, "E295", {"start": v(750.17, 7.55) * mm, "end": v(745.46, -36.62) * mm, "construction": true});
            skLineSegment(sketch, "E296", {"start": v(829.09, 0.1) * mm, "end": v(824.67, -53.6) * mm, "construction": true});
            skLineSegment(sketch, "E297", {"start": v(703.9, -7.33) * mm, "end": v(747.82, -14.54) * mm, "construction": true});
            skLineSegment(sketch, "E298", {"start": v(747.82, -14.54) * mm, "end": v(826.88, -26.76) * mm, "construction": true});
            skLineSegment(sketch, "E299", {"start": v(826.88, -26.76) * mm, "end": v(870.93, -33.16) * mm, "construction": true});
            skArc(sketch, "E300", {"start": v(746.44, -23.43) * mm, "mid": v(738.92, -13.16) * mm, "end": v(749.2, -5.64) * mm});
            skArc(sketch, "E301", {"start": v(825.5, -35.65) * mm, "mid": v(835.77, -28.13) * mm, "end": v(828.25, -17.86) * mm});
            skLineSegment(sketch, "E302", {"start": v(749.2, -5.64) * mm, "end": v(828.25, -17.86) * mm});
            skLineSegment(sketch, "E303", {"start": v(825.5, -35.65) * mm, "end": v(746.44, -23.43) * mm});
            skLineSegment(sketch, "E304", {"start": v(878.9, -33.7) * mm, "end": v(923.46, -35.94) * mm, "construction": true});
            skLineSegment(sketch, "E305", {"start": v(923.46, -35.94) * mm, "end": v(1003.39, -39.22) * mm, "construction": true});
            skLineSegment(sketch, "E306", {"start": v(1003.39, -39.22) * mm, "end": v(1047.97, -40.66) * mm, "construction": true});
            skLineSegment(sketch, "E307", {"start": v(925.02, -6.4) * mm, "end": v(921.9, -65.48) * mm, "construction": true});
            skLineSegment(sketch, "E308", {"start": v(1004.24, -9.64) * mm, "end": v(1002.54, -68.8) * mm, "construction": true});
            skArc(sketch, "E309", {"start": v(923.09, -44.93) * mm, "mid": v(914.46, -35.57) * mm, "end": v(923.83, -26.95) * mm});
            skArc(sketch, "E310", {"start": v(1003.02, -48.2) * mm, "mid": v(1012.38, -39.58) * mm, "end": v(1003.76, -30.22) * mm});
            skLineSegment(sketch, "E311", {"start": v(923.83, -26.95) * mm, "end": v(1003.76, -30.22) * mm});
            skLineSegment(sketch, "E312", {"start": v(1003.02, -48.2) * mm, "end": v(923.09, -44.93) * mm});
            skLineSegment(sketch, "E313.0", {"start": v(1098.97, -31) * mm, "end": v(1098.97, -47) * mm});
            skLineSegment(sketch, "E313.1", {"start": v(1059.97, -70.66) * mm, "end": v(1094.97, -70.66) * mm});
            skLineSegment(sketch, "E313.2", {"start": v(1090.97, -11) * mm, "end": v(1090.97, -31) * mm});
            skArc(sketch, "E314.0", {"start": v(-28, -70.9) * mm, "mid": v(0, -71) * mm, "end": v(28, -70.9) * mm});
            skArc(sketch, "E315.0", {"start": v(361.32, -70.9) * mm, "mid": v(389.32, -71) * mm, "end": v(417.3, -70.9) * mm});
            skLineSegment(sketch, "E316.0", {"start": v(1090.97, -51) * mm, "end": v(1094.97, -51) * mm});
            skLineSegment(sketch, "E316.1", {"start": v(1090.97, -51) * mm, "end": v(1083.97, -51) * mm});
            skLineSegment(sketch, "E316.2", {"start": v(1083.97, -51) * mm, "end": v(1083.97, -59) * mm});
            skLineSegment(sketch, "E316.4", {"start": v(1098.97, -63) * mm, "end": v(1098.97, -66.66) * mm});
            skPoint(sketch, "E317.visualSharp", {"position": v(-40, -70.81) * mm});
            skArc(sketch, "E317.filletArc", {"start": v(-45.18, -69.14) * mm, "mid": v(-41.61, -68.58) * mm, "end": v(-39.95, -65.37) * mm});
            skPoint(sketch, "E318.visualSharp", {"position": v(-32, -70.88) * mm});
            skArc(sketch, "E318.filletArc", {"start": v(-31.97, -66.87) * mm, "mid": v(-30.82, -69.72) * mm, "end": v(-28, -70.9) * mm});
            skPoint(sketch, "E319.visualSharp", {"position": v(32, -70.88) * mm});
            skArc(sketch, "E319.filletArc", {"start": v(28, -70.9) * mm, "mid": v(30.82, -69.72) * mm, "end": v(31.97, -66.87) * mm});
            skPoint(sketch, "E320.visualSharp", {"position": v(40, -70.81) * mm});
            skArc(sketch, "E320.filletArc", {"start": v(39.95, -65.37) * mm, "mid": v(41.61, -68.58) * mm, "end": v(45.18, -69.14) * mm});
            skPoint(sketch, "E321.visualSharp", {"position": v(349.32, -70.8) * mm});
            skArc(sketch, "E321.filletArc", {"start": v(344.78, -70.13) * mm, "mid": v(347.96, -69.21) * mm, "end": v(349.36, -66.21) * mm});
            skPoint(sketch, "E322.visualSharp", {"position": v(357.32, -70.87) * mm});
            skArc(sketch, "E322.filletArc", {"start": v(357.35, -66.86) * mm, "mid": v(358.5, -69.7) * mm, "end": v(361.32, -70.9) * mm});
            skPoint(sketch, "E323.visualSharp", {"position": v(421.32, -70.87) * mm});
            skArc(sketch, "E323.filletArc", {"start": v(417.3, -70.9) * mm, "mid": v(420.13, -69.7) * mm, "end": v(421.28, -66.86) * mm});
            skPoint(sketch, "E324.visualSharp", {"position": v(429.32, -70.8) * mm});
            skArc(sketch, "E324.filletArc", {"start": v(429.27, -66.21) * mm, "mid": v(430.67, -69.21) * mm, "end": v(433.85, -70.13) * mm});
            skPoint(sketch, "E325.visualSharp", {"position": v(868.9, -63.1) * mm});
            skArc(sketch, "E325.filletArc", {"start": v(864.38, -62.12) * mm, "mid": v(867.63, -61.4) * mm, "end": v(869.21, -58.48) * mm});
            skPoint(sketch, "E326.visualSharp", {"position": v(876.88, -63.63) * mm});
            skArc(sketch, "E326.filletArc", {"start": v(877.16, -59.53) * mm, "mid": v(878.17, -62.47) * mm, "end": v(880.99, -63.8) * mm});
            skPoint(sketch, "E327.visualSharp", {"position": v(1047.97, -70.66) * mm});
            skArc(sketch, "E327.filletArc", {"start": v(1043.8, -70.5) * mm, "mid": v(1046.74, -69.38) * mm, "end": v(1047.97, -66.5) * mm});
            skPoint(sketch, "E328.visualSharp", {"position": v(1055.97, -70.66) * mm});
            skArc(sketch, "E328.filletArc", {"start": v(1055.97, -66.66) * mm, "mid": v(1057.14, -69.5) * mm, "end": v(1059.97, -70.66) * mm});
            skPoint(sketch, "E329.visualSharp", {"position": v(1098.97, -59) * mm});
            skArc(sketch, "E329.filletArc", {"start": v(1098.97, -63) * mm, "mid": v(1097.8, -60.17) * mm, "end": v(1094.97, -59) * mm});
            skPoint(sketch, "E330.visualSharp", {"position": v(1098.97, -51) * mm});
            skArc(sketch, "E330.filletArc", {"start": v(1094.97, -51) * mm, "mid": v(1097.8, -49.83) * mm, "end": v(1098.97, -47) * mm});
            skPoint(sketch, "E331.visualSharp", {"position": v(1098.97, -70.66) * mm});
            skArc(sketch, "E331.filletArc", {"start": v(1094.97, -70.66) * mm, "mid": v(1097.8, -69.5) * mm, "end": v(1098.97, -66.66) * mm});
            skLineSegment(sketch, "E332.0", {"start": v(1083.97, -59) * mm, "end": v(1094.97, -59) * mm});
            skSolve(sketch);
        }
        {
            var Q0;
            Q0=qCreatedBy(makeId("Front.planeOp"),FACE);
            var sketch = newSketch(context, id + "F11", { "sketchPlane" : qUnion([Q0])});
            skPoint(sketch, "E333.2", {"position": v(1098.97, 0) * mm});
            skLineSegment(sketch, "E334", {"start": v(1098.97, 0) * mm, "end": v(1098.97, -20) * mm, "construction": true});
            skPoint(sketch, "E335.0", {"position": v(389.32, 0) * mm});
            skPoint(sketch, "E335.1", {"position": v(393.79, 0.5) * mm});
            skCircle(sketch, "E336", {"center": v(389.32, 0) * mm, "radius": 4.5 * mm});
            skPoint(sketch, "E337.0", {"position": v(0, 0) * mm});
            skPoint(sketch, "E337.1", {"position": v(4.47, 0.5) * mm});
            skCircle(sketch, "E338", {"center": v(0, 0) * mm, "radius": 4.5 * mm});
            skCircle(sketch, "E339.MirrorC", {"center": v(1808.62, 0) * mm, "radius": 4.5 * mm});
            skCircle(sketch, "E340.MirrorC", {"center": v(2197.94, 0) * mm, "radius": 4.5 * mm});
            skLineSegment(sketch, "E341.bottom", {"start": v(-162.5, 20) * mm, "end": v(2360.44, 20) * mm});
            skLineSegment(sketch, "E341.top", {"start": v(-162.5, -20) * mm, "end": v(2360.44, -20) * mm});
            skLineSegment(sketch, "E341.left", {"start": v(-162.5, 20) * mm, "end": v(-162.5, -20) * mm, "construction": true});
            skLineSegment(sketch, "E341.right", {"start": v(2360.44, 20) * mm, "end": v(2360.44, -20) * mm, "construction": true});
            skLineSegment(sketch, "E342", {"start": v(0, 0) * mm, "end": v(389.32, 0) * mm, "construction": true});
            skLineSegment(sketch, "E343", {"start": v(619.32, 20) * mm, "end": v(619.32, -20) * mm});
            skLineSegment(sketch, "E344.MirrorCS", {"start": v(659.32, 20) * mm, "end": v(659.32, -20) * mm});
            skArc(sketch, "E345", {"start": v(-162.5, -20) * mm, "mid": v(-182.5, 0) * mm, "end": v(-162.5, 20) * mm});
            skArc(sketch, "E346.MirrorCS", {"start": v(2360.44, -20) * mm, "mid": v(2380.44, 0) * mm, "end": v(2360.44, 20) * mm});
            skCircle(sketch, "E347", {"center": v(-162.5, 0) * mm, "radius": 4.5 * mm});
            skCircle(sketch, "E348.MirrorC", {"center": v(2360.44, 0) * mm, "radius": 4.5 * mm});
            skLineSegment(sketch, "E349", {"start": v(639.32, 20) * mm, "end": v(639.32, -20) * mm, "construction": true});
            skLineSegment(sketch, "E350.MirrorCS", {"start": v(1578.62, 20) * mm, "end": v(1578.62, -20) * mm});
            skLineSegment(sketch, "E351.MirrorCS", {"start": v(1538.62, 20) * mm, "end": v(1538.62, -20) * mm});
            skSolve(sketch);
        }
        {
            var Q0;
            Q0=sQuery(id+"F9.wireOp",EDGE,"E112");
            cPlane(context, id + "F12", {"entities" : qUnion([Q0]), "cplaneType" : CPlaneType.LINE_ANGLE, "offset" : 25 * mm, "angle" : 0 * degree, "width" : 150 * mm, "height" : 150 * mm});
        }
        {
            var Q0;
            Q0=qCreatedBy(id+"F12.planeOp",FACE);
            var sketch = newSketch(context, id + "F13", { "sketchPlane" : qUnion([Q0])});
            skPoint(sketch, "E352.0", {"position": v(0, -41.15) * mm});
            skPoint(sketch, "E353.0", {"position": v(0, -71.15) * mm});
            skLineSegment(sketch, "E354", {"start": v(0, -41.15) * mm, "end": v(8, -41.15) * mm});
            skLineSegment(sketch, "E355", {"start": v(8, -41.15) * mm, "end": v(8, -11.15) * mm});
            skLineSegment(sketch, "E356", {"start": v(0, -71.15) * mm, "end": v(0, -41.15) * mm});
            skLineSegment(sketch, "E357", {"start": v(0, -71.15) * mm, "end": v(394.67, -71.15) * mm});
            skLineSegment(sketch, "E358", {"start": v(600, -11.17) * mm, "end": v(600, -71.17) * mm, "construction": true});
            skLineSegment(sketch, "E359", {"start": v(394.67, -41.15) * mm, "end": v(402.67, -41.15) * mm});
            skLineSegment(sketch, "E360.MirrorCS", {"start": v(805.33, -41.15) * mm, "end": v(797.33, -41.15) * mm});
            skLineSegment(sketch, "E361.MirrorCS", {"start": v(1192, -41.15) * mm, "end": v(1192, -11.15) * mm});
            skLineSegment(sketch, "E362.MirrorCS", {"start": v(1200, -71.15) * mm, "end": v(1200, -41.15) * mm});
            skLineSegment(sketch, "E363.MirrorCS", {"start": v(1200, -41.15) * mm, "end": v(1192, -41.15) * mm});
            skLineSegment(sketch, "E364", {"start": v(394.67, -41.15) * mm, "end": v(394.67, -71.15) * mm});
            skLineSegment(sketch, "E365", {"start": v(402.67, -41.15) * mm, "end": v(402.67, -71.15) * mm});
            skLineSegment(sketch, "E366.MirrorCS", {"start": v(805.33, -41.15) * mm, "end": v(805.33, -71.15) * mm});
            skLineSegment(sketch, "E367.MirrorCS", {"start": v(797.33, -41.15) * mm, "end": v(797.33, -71.15) * mm});
            skLineSegment(sketch, "E368.MirrorCS", {"start": v(1200, -71.15) * mm, "end": v(805.33, -71.15) * mm});
            skLineSegment(sketch, "E369", {"start": v(402.67, -71.15) * mm, "end": v(797.33, -71.15) * mm});
            skLineSegment(sketch, "E370", {"start": v(8, -11.15) * mm, "end": v(1192, -11.15) * mm});
            skPoint(sketch, "E371.0", {"position": v(0, -11.15) * mm});
            skSolve(sketch);
        }
        {
            var Q0;
            Q0=sQuery(id+"F9.wireOp",EDGE,"E116");
            cPlane(context, id + "F14", {"entities" : qUnion([Q0]), "cplaneType" : CPlaneType.LINE_ANGLE, "offset" : 25 * mm, "angle" : 0 * degree, "width" : 150 * mm, "height" : 150 * mm});
        }
        {
            var Q0;
            Q0=qCreatedBy(id+"F14.planeOp",FACE);
            var sketch = newSketch(context, id + "F15", { "sketchPlane" : qUnion([Q0])});
            skPoint(sketch, "E372.0", {"position": v(0, -12.42) * mm});
            skPoint(sketch, "E372.1", {"position": v(0, -52.42) * mm});
            skPoint(sketch, "E372.2", {"position": v(0, -32.42) * mm});
            skLineSegment(sketch, "E373", {"start": v(0, -32.42) * mm, "end": v(8, -32.42) * mm});
            skLineSegment(sketch, "E374", {"start": v(0, -12.42) * mm, "end": v(394.67, -12.42) * mm});
            skPoint(sketch, "E375.0", {"position": v(8, -11.77) * mm});
            skLineSegment(sketch, "E376.0", {"start": v(600, -11.8) * mm, "end": v(600, -71.79) * mm, "construction": true});
            skLineSegment(sketch, "E377.MirrorCS", {"start": v(1200, -32.42) * mm, "end": v(1192, -32.42) * mm});
            skLineSegment(sketch, "E378", {"start": v(8, -52.42) * mm, "end": v(1192, -52.42) * mm});
            skLineSegment(sketch, "E379.top", {"start": v(394.67, -32.42) * mm, "end": v(402.67, -32.42) * mm});
            skPoint(sketch, "E380.0", {"position": v(394.67, -71.76) * mm});
            skPoint(sketch, "E380.1", {"position": v(402.67, -71.76) * mm});
            skLineSegment(sketch, "E381", {"start": v(0, -32.42) * mm, "end": v(0, -12.42) * mm});
            skLineSegment(sketch, "E382", {"start": v(8, -32.42) * mm, "end": v(8, -52.42) * mm});
            skLineSegment(sketch, "E383", {"start": v(402.67, -32.42) * mm, "end": v(402.67, -12.42) * mm});
            skLineSegment(sketch, "E384", {"start": v(394.67, -12.42) * mm, "end": v(394.67, -32.42) * mm});
            skLineSegment(sketch, "E385.trimOffspring", {"start": v(402.67, -12.42) * mm, "end": v(797.33, -12.42) * mm});
            skLineSegment(sketch, "E386.MirrorCS", {"start": v(797.33, -32.42) * mm, "end": v(797.33, -12.42) * mm});
            skLineSegment(sketch, "E387.MirrorCS", {"start": v(805.33, -12.42) * mm, "end": v(805.33, -32.42) * mm});
            skLineSegment(sketch, "E388.MirrorCS", {"start": v(1192, -32.42) * mm, "end": v(1192, -52.42) * mm});
            skLineSegment(sketch, "E389.MirrorCS", {"start": v(1200, -32.42) * mm, "end": v(1200, -12.42) * mm});
            skLineSegment(sketch, "E390.MirrorCS", {"start": v(805.33, -32.42) * mm, "end": v(797.33, -32.42) * mm});
            skLineSegment(sketch, "E391.trimOffspring", {"start": v(805.33, -12.42) * mm, "end": v(1200, -12.42) * mm});
            skSolve(sketch);
        }
        {
            var Q0;
            Q0=sQuery(id+"F9.wireOp",EDGE,"E141");
            cPlane(context, id + "F16", {"entities" : qUnion([Q0]), "cplaneType" : CPlaneType.LINE_ANGLE, "offset" : 25 * mm, "angle" : 0 * degree, "width" : 150 * mm, "height" : 150 * mm});
        }
        {
            var Q0;
            Q0=qCreatedBy(id+"F16.planeOp",FACE);
            var sketch = newSketch(context, id + "F17", { "sketchPlane" : qUnion([Q0])});
            skPoint(sketch, "E392.0", {"position": v(0, -67.5) * mm});
            skPoint(sketch, "E392.1", {"position": v(0, -7.5) * mm});
            skPoint(sketch, "E392.2", {"position": v(0, -37.5) * mm});
            skLineSegment(sketch, "E393.0", {"start": v(-600, -11.2) * mm, "end": v(-600, -71.2) * mm, "construction": true});
            skPoint(sketch, "E394.0", {"position": v(-8, -11.18) * mm});
            skLineSegment(sketch, "E395", {"start": v(0, -67.5) * mm, "end": v(0, -37.5) * mm});
            skLineSegment(sketch, "E396", {"start": v(-8, -37.5) * mm, "end": v(-8, -7.5) * mm});
            skLineSegment(sketch, "E397", {"start": v(0, -37.5) * mm, "end": v(-8, -37.5) * mm});
            skLineSegment(sketch, "E398.MirrorCS", {"start": v(-1192, -37.5) * mm, "end": v(-1192, -7.5) * mm});
            skLineSegment(sketch, "E399.MirrorCS", {"start": v(-1200, -67.5) * mm, "end": v(-1200, -37.5) * mm});
            skLineSegment(sketch, "E400.MirrorCS", {"start": v(-1200, -37.5) * mm, "end": v(-1192, -37.5) * mm});
            skLineSegment(sketch, "E401", {"start": v(-1200, -67.5) * mm, "end": v(-805.33, -67.5) * mm});
            skLineSegment(sketch, "E402", {"start": v(-1192, -7.5) * mm, "end": v(-8, -7.5) * mm});
            skLineSegment(sketch, "E403.bottom", {"start": v(-394.67, -37.5) * mm, "end": v(-402.67, -37.5) * mm});
            skLineSegment(sketch, "E403.left", {"start": v(-394.67, -37.5) * mm, "end": v(-394.67, -67.5) * mm});
            skLineSegment(sketch, "E403.right", {"start": v(-402.67, -37.5) * mm, "end": v(-402.67, -67.5) * mm});
            skLineSegment(sketch, "E404.trimOffspring", {"start": v(-394.67, -67.5) * mm, "end": v(0, -67.5) * mm});
            skLineSegment(sketch, "E405.MirrorCS", {"start": v(-805.33, -37.5) * mm, "end": v(-805.33, -67.5) * mm});
            skLineSegment(sketch, "E406.MirrorCS", {"start": v(-805.33, -37.5) * mm, "end": v(-797.33, -37.5) * mm});
            skLineSegment(sketch, "E407.MirrorCS", {"start": v(-797.33, -37.5) * mm, "end": v(-797.33, -67.5) * mm});
            skLineSegment(sketch, "E408.trimOffspring", {"start": v(-797.33, -67.5) * mm, "end": v(-402.67, -67.5) * mm});
            skPoint(sketch, "E409.0", {"position": v(-394.67, -71.18) * mm});
            skPoint(sketch, "E409.1", {"position": v(-402.67, -71.18) * mm});
            skSolve(sketch);
        }
        {
            var Q0;
            Q0=sQuery(id+"F9.wireOp",EDGE,"E142");
            cPlane(context, id + "F18", {"entities" : qUnion([Q0]), "cplaneType" : CPlaneType.LINE_ANGLE, "offset" : 25 * mm, "angle" : 0 * degree, "width" : 150 * mm, "height" : 150 * mm});
        }
        {
            var Q0;
            Q0=qCreatedBy(id+"F18.planeOp",FACE);
            var sketch = newSketch(context, id + "F19", { "sketchPlane" : qUnion([Q0])});
            skPoint(sketch, "E410.0", {"position": v(0, 5.4) * mm});
            skPoint(sketch, "E410.1", {"position": v(0, -34.6) * mm});
            skPoint(sketch, "E410.2", {"position": v(0, -14.6) * mm});
            skLineSegment(sketch, "E411.0", {"start": v(-600, -12.94) * mm, "end": v(-600, -72.86) * mm, "construction": true});
            skPoint(sketch, "E412.0", {"position": v(-8, -12.92) * mm});
            skLineSegment(sketch, "E413", {"start": v(-8, -14.6) * mm, "end": v(0, -14.6) * mm});
            skLineSegment(sketch, "E414", {"start": v(0, 5.4) * mm, "end": v(-394.67, 5.4) * mm});
            skLineSegment(sketch, "E415.MirrorCS", {"start": v(-1192, -14.6) * mm, "end": v(-1200, -14.6) * mm});
            skLineSegment(sketch, "E416.top", {"start": v(-394.67, -14.6) * mm, "end": v(-402.67, -14.6) * mm});
            skLineSegment(sketch, "E416.left", {"start": v(-394.67, -14.6) * mm, "end": v(-394.67, 5.4) * mm});
            skLineSegment(sketch, "E416.right", {"start": v(-402.67, -14.6) * mm, "end": v(-402.67, 5.4) * mm});
            skPoint(sketch, "E417.0", {"position": v(-394.67, -72.84) * mm});
            skPoint(sketch, "E417.1", {"position": v(-402.67, -72.84) * mm});
            skLineSegment(sketch, "E418", {"start": v(0, -14.6) * mm, "end": v(0, 5.4) * mm});
            skLineSegment(sketch, "E419", {"start": v(-8, -14.6) * mm, "end": v(-8, -34.6) * mm});
            skLineSegment(sketch, "E420.MirrorCS", {"start": v(-797.33, -14.6) * mm, "end": v(-797.33, 5.4) * mm});
            skLineSegment(sketch, "E421.MirrorCS", {"start": v(-805.33, -14.6) * mm, "end": v(-805.33, 5.4) * mm});
            skLineSegment(sketch, "E422.MirrorCS", {"start": v(-805.33, -14.6) * mm, "end": v(-797.33, -14.6) * mm});
            skLineSegment(sketch, "E423.MirrorCS", {"start": v(-1200, 5.4) * mm, "end": v(-805.33, 5.4) * mm});
            skLineSegment(sketch, "E424.MirrorCS", {"start": v(-1192, -14.6) * mm, "end": v(-1192, -34.6) * mm});
            skLineSegment(sketch, "E425.MirrorCS", {"start": v(-1200, -14.6) * mm, "end": v(-1200, 5.4) * mm});
            skLineSegment(sketch, "E426", {"start": v(-797.33, 5.4) * mm, "end": v(-402.67, 5.4) * mm});
            skLineSegment(sketch, "E427", {"start": v(-1192, -34.6) * mm, "end": v(-8, -34.6) * mm});
            skSolve(sketch);
        }
        {
            var Q0;
            Q0=sQuery(id+"F9.wireOp",EDGE,"E181");
            cPlane(context, id + "F20", {"entities" : qUnion([Q0]), "cplaneType" : CPlaneType.LINE_ANGLE, "offset" : 25 * mm, "angle" : 0 * degree, "width" : 150 * mm, "height" : 150 * mm});
        }
        {
            var Q0;
            Q0=sQuery(id+"F9.wireOp",EDGE,"E190");
            cPlane(context, id + "F21", {"entities" : qUnion([Q0]), "cplaneType" : CPlaneType.LINE_ANGLE, "offset" : 25 * mm, "angle" : 0 * degree, "width" : 150 * mm, "height" : 150 * mm});
        }
        {
            var Q0;
            Q0=sQuery(id+"F9.wireOp",EDGE,"E177");
            cPlane(context, id + "F22", {"entities" : qUnion([Q0]), "cplaneType" : CPlaneType.LINE_ANGLE, "offset" : 25 * mm, "angle" : 0 * degree, "width" : 150 * mm, "height" : 150 * mm});
        }
        {
            var Q0;
            Q0=sQuery(id+"F9.wireOp",EDGE,"E219");
            cPlane(context, id + "F23", {"entities" : qUnion([Q0]), "cplaneType" : CPlaneType.LINE_ANGLE, "offset" : 25 * mm, "angle" : 0 * degree, "width" : 150 * mm, "height" : 150 * mm});
        }
        {
            var Q0;
            Q0=qCreatedBy(id+"F23.planeOp",FACE);
            var sketch = newSketch(context, id + "F24", { "sketchPlane" : qUnion([Q0])});
            skPoint(sketch, "E428.0", {"position": v(0, -10.66) * mm});
            skPoint(sketch, "E428.1", {"position": v(0, -40.66) * mm});
            skPoint(sketch, "E428.2", {"position": v(0, -70.66) * mm});
            skPoint(sketch, "E429.0", {"position": v(402.67, -70.85) * mm});
            skPoint(sketch, "E429.1", {"position": v(394.67, -70.85) * mm});
            skPoint(sketch, "E429.2", {"position": v(8, -40.85) * mm});
            skLineSegment(sketch, "E430", {"start": v(0, -70.66) * mm, "end": v(0, -40.66) * mm});
            skLineSegment(sketch, "E431", {"start": v(0, -40.66) * mm, "end": v(8, -40.66) * mm});
            skLineSegment(sketch, "E432", {"start": v(8, -40.66) * mm, "end": v(8, -10.66) * mm});
            skLineSegment(sketch, "E433", {"start": v(8, -10.66) * mm, "end": v(394.67, -10.66) * mm});
            skLineSegment(sketch, "E434", {"start": v(394.67, -10.66) * mm, "end": v(394.67, -40.66) * mm});
            skLineSegment(sketch, "E435", {"start": v(394.67, -40.66) * mm, "end": v(402.67, -40.66) * mm});
            skLineSegment(sketch, "E436", {"start": v(402.67, -40.66) * mm, "end": v(402.67, -10.66) * mm});
            skLineSegment(sketch, "E437.0", {"start": v(600, -10.87) * mm, "end": v(600, -70.87) * mm, "construction": true});
            skLineSegment(sketch, "E438.MirrorCS", {"start": v(797.33, -40.66) * mm, "end": v(797.33, -10.66) * mm});
            skLineSegment(sketch, "E439.MirrorCS", {"start": v(805.33, -10.66) * mm, "end": v(805.33, -40.66) * mm});
            skLineSegment(sketch, "E440.MirrorCS", {"start": v(805.33, -40.66) * mm, "end": v(797.33, -40.66) * mm});
            skLineSegment(sketch, "E441.MirrorCS", {"start": v(1192, -10.66) * mm, "end": v(805.33, -10.66) * mm});
            skLineSegment(sketch, "E442.MirrorCS", {"start": v(1192, -40.66) * mm, "end": v(1192, -10.66) * mm});
            skLineSegment(sketch, "E443.MirrorCS", {"start": v(1200, -70.66) * mm, "end": v(1200, -40.66) * mm});
            skLineSegment(sketch, "E444.MirrorCS", {"start": v(1200, -40.66) * mm, "end": v(1192, -40.66) * mm});
            skLineSegment(sketch, "E445", {"start": v(797.33, -10.66) * mm, "end": v(402.67, -10.66) * mm});
            skLineSegment(sketch, "E446", {"start": v(1200, -70.66) * mm, "end": v(1002.67, -70.66) * mm});
            skLineSegment(sketch, "E447.MirrorCS", {"start": v(201.33, -10.66) * mm, "end": v(201.33, -63.16) * mm, "construction": true});
            skLineSegment(sketch, "E448", {"start": v(205.33, -70.66) * mm, "end": v(205.33, -63.16) * mm});
            skLineSegment(sketch, "E449", {"start": v(205.33, -63.16) * mm, "end": v(197.33, -63.16) * mm});
            skLineSegment(sketch, "E450", {"start": v(197.33, -63.16) * mm, "end": v(197.33, -70.66) * mm});
            skLineSegment(sketch, "E451.trimOffspring", {"start": v(197.33, -70.66) * mm, "end": v(0, -70.66) * mm});
            skLineSegment(sketch, "E452", {"start": v(604, -70.66) * mm, "end": v(604, -63.16) * mm});
            skLineSegment(sketch, "E453", {"start": v(604, -63.16) * mm, "end": v(596, -63.16) * mm});
            skLineSegment(sketch, "E454", {"start": v(596, -63.16) * mm, "end": v(596, -70.66) * mm});
            skLineSegment(sketch, "E455.trimOffspring", {"start": v(596, -70.66) * mm, "end": v(205.33, -70.66) * mm});
            skLineSegment(sketch, "E456.MirrorCS", {"start": v(994.67, -70.66) * mm, "end": v(994.67, -63.16) * mm});
            skLineSegment(sketch, "E457.MirrorCS", {"start": v(994.67, -63.16) * mm, "end": v(1002.67, -63.16) * mm});
            skLineSegment(sketch, "E458.MirrorCS", {"start": v(1002.67, -63.16) * mm, "end": v(1002.67, -70.66) * mm});
            skLineSegment(sketch, "E459.trimOffspring", {"start": v(994.67, -70.66) * mm, "end": v(604, -70.66) * mm});
            skPoint(sketch, "E460.0", {"position": v(0, -63.16) * mm});
            skSolve(sketch);
        }
        {
            var Q0;
            Q0=qCreatedBy(id+"F20.planeOp",FACE);
            var sketch = newSketch(context, id + "F25", { "sketchPlane" : qUnion([Q0])});
            skPoint(sketch, "E461.0", {"position": v(0, 97.6) * mm});
            skPoint(sketch, "E461.1", {"position": v(0, 57.6) * mm});
            skPoint(sketch, "E461.2", {"position": v(0, 77.6) * mm});
            skPoint(sketch, "E462.0", {"position": v(402.67, -44.86) * mm});
            skPoint(sketch, "E462.1", {"position": v(394.67, -44.86) * mm});
            skPoint(sketch, "E463.0", {"position": v(8, -44.86) * mm});
            skLineSegment(sketch, "E464", {"start": v(0, 77.6) * mm, "end": v(0, 97.6) * mm});
            skLineSegment(sketch, "E465", {"start": v(8, 77.6) * mm, "end": v(0, 77.6) * mm});
            skLineSegment(sketch, "E466", {"start": v(8, 57.6) * mm, "end": v(8, 77.6) * mm});
            skLineSegment(sketch, "E467", {"start": v(394.67, 77.6) * mm, "end": v(402.67, 77.6) * mm});
            skLineSegment(sketch, "E468.0", {"start": v(600, -15.07) * mm, "end": v(600, -74.7) * mm, "construction": true});
            skLineSegment(sketch, "E469.MirrorCS", {"start": v(1192, 57.6) * mm, "end": v(1192, 77.6) * mm});
            skLineSegment(sketch, "E470.MirrorCS", {"start": v(805.33, 77.6) * mm, "end": v(797.33, 77.6) * mm});
            skLineSegment(sketch, "E471.MirrorCS", {"start": v(1192, 57.6) * mm, "end": v(8, 57.6) * mm});
            skLineSegment(sketch, "E472.MirrorCS", {"start": v(1192, 77.6) * mm, "end": v(1200, 77.6) * mm});
            skLineSegment(sketch, "E473.MirrorCS", {"start": v(1200, 77.6) * mm, "end": v(1200, 97.6) * mm});
            skLineSegment(sketch, "E474", {"start": v(1200, 97.6) * mm, "end": v(805.33, 97.6) * mm});
            skLineSegment(sketch, "E475", {"start": v(394.67, 97.6) * mm, "end": v(394.67, 77.6) * mm});
            skLineSegment(sketch, "E476", {"start": v(402.67, 77.6) * mm, "end": v(402.67, 97.6) * mm});
            skLineSegment(sketch, "E477.trimOffspring", {"start": v(394.67, 97.6) * mm, "end": v(0, 97.6) * mm});
            skLineSegment(sketch, "E478.MirrorCS", {"start": v(797.33, 77.6) * mm, "end": v(797.33, 97.6) * mm});
            skLineSegment(sketch, "E479.MirrorCS", {"start": v(805.33, 97.6) * mm, "end": v(805.33, 77.6) * mm});
            skLineSegment(sketch, "E480.trimOffspring", {"start": v(797.33, 97.6) * mm, "end": v(402.67, 97.6) * mm});
            skSolve(sketch);
        }
        {
            var Q0;
            Q0=qCreatedBy(id+"F21.planeOp",FACE);
            var sketch = newSketch(context, id + "F26", { "sketchPlane" : qUnion([Q0])});
            skPoint(sketch, "E481.0", {"position": v(0, -4.3) * mm});
            skPoint(sketch, "E481.1", {"position": v(0, 55.7) * mm});
            skPoint(sketch, "E481.2", {"position": v(0, 25.7) * mm});
            skLineSegment(sketch, "E482.0", {"start": v(600, -13.24) * mm, "end": v(600, -73.14) * mm, "construction": true});
            skPoint(sketch, "E483.0", {"position": v(402.67, -73.11) * mm});
            skPoint(sketch, "E483.1", {"position": v(394.67, -73.11) * mm});
            skPoint(sketch, "E484.0", {"position": v(8, -43.17) * mm});
            skLineSegment(sketch, "E485", {"start": v(0, -4.3) * mm, "end": v(0, 25.7) * mm});
            skLineSegment(sketch, "E486", {"start": v(8, 25.7) * mm, "end": v(8, 55.7) * mm});
            skLineSegment(sketch, "E487", {"start": v(8, 25.7) * mm, "end": v(0, 25.7) * mm});
            skLineSegment(sketch, "E488", {"start": v(0, -4.3) * mm, "end": v(394.67, -4.3) * mm});
            skLineSegment(sketch, "E489", {"start": v(394.67, -4.3) * mm, "end": v(394.67, 25.7) * mm});
            skLineSegment(sketch, "E490", {"start": v(394.67, 25.7) * mm, "end": v(402.67, 25.7) * mm});
            skLineSegment(sketch, "E491", {"start": v(402.67, 25.7) * mm, "end": v(402.67, -4.3) * mm});
            skLineSegment(sketch, "E492.MirrorCS", {"start": v(805.33, 25.7) * mm, "end": v(797.33, 25.7) * mm});
            skLineSegment(sketch, "E493.MirrorCS", {"start": v(797.33, 25.7) * mm, "end": v(797.33, -4.3) * mm});
            skLineSegment(sketch, "E494.MirrorCS", {"start": v(805.33, -4.3) * mm, "end": v(805.33, 25.7) * mm});
            skLineSegment(sketch, "E495.MirrorCS", {"start": v(1192, 25.7) * mm, "end": v(1192, 55.7) * mm});
            skLineSegment(sketch, "E496.MirrorCS", {"start": v(1192, 25.7) * mm, "end": v(1200, 25.7) * mm});
            skLineSegment(sketch, "E497.MirrorCS", {"start": v(1200, -4.3) * mm, "end": v(1200, 25.7) * mm});
            skLineSegment(sketch, "E498.MirrorCS", {"start": v(1200, -4.3) * mm, "end": v(805.33, -4.3) * mm});
            skLineSegment(sketch, "E499", {"start": v(797.33, -4.3) * mm, "end": v(402.67, -4.3) * mm});
            skLineSegment(sketch, "E500", {"start": v(8, 55.7) * mm, "end": v(1192, 55.7) * mm});
            skSolve(sketch);
        }
        {
            var Q0;
            Q0=qCreatedBy(id+"F22.planeOp",FACE);
            var sketch = newSketch(context, id + "F27", { "sketchPlane" : qUnion([Q0])});
            skPoint(sketch, "E501.0", {"position": v(0, -11) * mm});
            skPoint(sketch, "E501.1", {"position": v(0, -31) * mm});
            skPoint(sketch, "E501.2", {"position": v(0, -51) * mm});
            skPoint(sketch, "E502.0", {"position": v(402.67, -70.85) * mm});
            skPoint(sketch, "E502.1", {"position": v(394.67, -70.85) * mm});
            skPoint(sketch, "E502.2", {"position": v(8, -40.85) * mm});
            skLineSegment(sketch, "E502.3", {"start": v(600, -10.87) * mm, "end": v(600, -70.87) * mm, "construction": true});
            skLineSegment(sketch, "E503", {"start": v(0, -31) * mm, "end": v(8, -31) * mm});
            skLineSegment(sketch, "E504", {"start": v(8, -51) * mm, "end": v(8, -31) * mm});
            skLineSegment(sketch, "E505", {"start": v(0, -11) * mm, "end": v(394.67, -11) * mm});
            skLineSegment(sketch, "E506", {"start": v(394.67, -31) * mm, "end": v(394.67, -11) * mm});
            skLineSegment(sketch, "E507", {"start": v(394.67, -31) * mm, "end": v(402.67, -31) * mm});
            skLineSegment(sketch, "E508", {"start": v(402.67, -11) * mm, "end": v(402.67, -31) * mm});
            skLineSegment(sketch, "E509.MirrorCS", {"start": v(797.33, -11) * mm, "end": v(797.33, -31) * mm});
            skLineSegment(sketch, "E510.MirrorCS", {"start": v(805.33, -31) * mm, "end": v(805.33, -11) * mm});
            skLineSegment(sketch, "E511.MirrorCS", {"start": v(1200, -11) * mm, "end": v(805.33, -11) * mm});
            skLineSegment(sketch, "E512.MirrorCS", {"start": v(805.33, -31) * mm, "end": v(797.33, -31) * mm});
            skLineSegment(sketch, "E513.MirrorCS", {"start": v(1192, -51) * mm, "end": v(1192, -31) * mm});
            skLineSegment(sketch, "E514.MirrorCS", {"start": v(1200, -31) * mm, "end": v(1192, -31) * mm});
            skLineSegment(sketch, "E515", {"start": v(1192, -51) * mm, "end": v(8, -51) * mm});
            skLineSegment(sketch, "E516", {"start": v(797.33, -11) * mm, "end": v(402.67, -11) * mm});
            skLineSegment(sketch, "E517", {"start": v(0, -31) * mm, "end": v(0, -11) * mm});
            skLineSegment(sketch, "E518", {"start": v(1200, -31) * mm, "end": v(1200, -11) * mm});
            skSolve(sketch);
        }
        {
            var Q0;
            Q0=sQuery(id+"F13.wireOp",VERTEX,"E359.start");
            var Q1;
            Q1=qCreatedBy(makeId("Front.planeOp"),FACE);
            cPlane(context, id + "F28", {"entities" : qUnion([Q0, Q1]), "cplaneType" : CPlaneType.PLANE_POINT, "offset" : 25 * mm, "width" : 150 * mm, "height" : 150 * mm});
        }
        {
            var Q0;
            Q0=qCreatedBy(id+"F28.planeOp",FACE);
            var sketch = newSketch(context, id + "F29", { "sketchPlane" : qUnion([Q0])});
            skLineSegment(sketch, "E519.0", {"start": v(-51.16, -29.77) * mm, "end": v(-90.6, -23.05) * mm});
            skLineSegment(sketch, "E519.1", {"start": v(-93.62, -40.8) * mm, "end": v(-54.19, -47.51) * mm});
            skArc(sketch, "E519.2", {"start": v(-93.62, -40.8) * mm, "mid": v(-100.98, -30.4) * mm, "end": v(-90.6, -23.05) * mm});
            skArc(sketch, "E519.3", {"start": v(-54.19, -47.51) * mm, "mid": v(-43.8, -40.15) * mm, "end": v(-51.16, -29.77) * mm});
            skLineSegment(sketch, "E519.4", {"start": v(93.62, -40.8) * mm, "end": v(54.19, -47.51) * mm});
            skLineSegment(sketch, "E519.5", {"start": v(51.16, -29.77) * mm, "end": v(90.6, -23.05) * mm});
            skArc(sketch, "E519.6", {"start": v(54.19, -47.51) * mm, "mid": v(43.8, -40.15) * mm, "end": v(51.16, -29.77) * mm});
            skArc(sketch, "E519.7", {"start": v(93.62, -40.8) * mm, "mid": v(100.98, -30.4) * mm, "end": v(90.6, -23.05) * mm});
            skArc(sketch, "E520.0", {"start": v(-112.5, -9.47) * mm, "mid": v(-78, -10.27) * mm, "end": v(-43.48, -10.77) * mm});
            skLineSegment(sketch, "E520.1", {"start": v(-112.5, -9.47) * mm, "end": v(-113.02, -29.47) * mm});
            skLineSegment(sketch, "E520.2", {"start": v(-105.55, -49.67) * mm, "end": v(-105.03, -29.68) * mm});
            skLineSegment(sketch, "E520.3", {"start": v(-113.02, -29.47) * mm, "end": v(-105.03, -29.68) * mm});
            skLineSegment(sketch, "E520.4", {"start": v(-105.55, -49.67) * mm, "end": v(-40, -70.81) * mm});
            skLineSegment(sketch, "E520.6", {"start": v(-39.74, -40.81) * mm, "end": v(-31.74, -40.88) * mm});
            skLineSegment(sketch, "E520.7", {"start": v(-39.74, -40.81) * mm, "end": v(-39.52, -14.8) * mm});
            skLineSegment(sketch, "E520.8", {"start": v(-32, -70.88) * mm, "end": v(-32, -70.78) * mm});
            skArc(sketch, "E521.trimOffspring", {"start": v(-27.5, -10.9) * mm, "mid": v(0, -11) * mm, "end": v(27.5, -10.9) * mm});
            skLineSegment(sketch, "E522.trimOffspring", {"start": v(-31.74, -40.88) * mm, "end": v(-31.52, -14.87) * mm});
            skLineSegment(sketch, "E523.0", {"start": v(0, 0) * mm, "end": v(0, -6) * mm, "construction": true});
            skLineSegment(sketch, "E524.MirrorCS", {"start": v(112.5, -9.47) * mm, "end": v(113.02, -29.47) * mm});
            skLineSegment(sketch, "E525.MirrorCS", {"start": v(113.02, -29.47) * mm, "end": v(105.03, -29.68) * mm});
            skLineSegment(sketch, "E526.MirrorCS", {"start": v(105.55, -49.67) * mm, "end": v(105.03, -29.68) * mm});
            skLineSegment(sketch, "E527.MirrorCS", {"start": v(39.74, -40.81) * mm, "end": v(39.52, -14.8) * mm});
            skLineSegment(sketch, "E528.MirrorCS", {"start": v(39.74, -40.81) * mm, "end": v(31.74, -40.88) * mm});
            skLineSegment(sketch, "E529.MirrorCS", {"start": v(31.74, -40.88) * mm, "end": v(31.52, -14.87) * mm});
            skLineSegment(sketch, "E530.MirrorCS", {"start": v(105.55, -49.67) * mm, "end": v(40, -70.81) * mm});
            skArc(sketch, "E531.trimOffspring", {"start": v(43.48, -10.77) * mm, "mid": v(78, -10.27) * mm, "end": v(112.5, -9.47) * mm});
            skLineSegment(sketch, "E532.0", {"start": v(389.32, 0) * mm, "end": v(389.32, -6) * mm, "construction": true});
            skArc(sketch, "E533.0", {"start": v(164.02, -4.25) * mm, "mid": v(254.91, -8.6) * mm, "end": v(345.9, -10.75) * mm});
            skLineSegment(sketch, "E533.1", {"start": v(164.02, -4.25) * mm, "end": v(162.84, -24.21) * mm});
            skLineSegment(sketch, "E533.2", {"start": v(162.84, -24.21) * mm, "end": v(170.83, -24.68) * mm});
            skLineSegment(sketch, "E533.3", {"start": v(169.65, -44.65) * mm, "end": v(170.83, -24.68) * mm});
            skLineSegment(sketch, "E533.4", {"start": v(169.65, -44.65) * mm, "end": v(349.32, -70.8) * mm});
            skLineSegment(sketch, "E533.6", {"start": v(349.84, -14.79) * mm, "end": v(349.6, -40.8) * mm});
            skLineSegment(sketch, "E533.7", {"start": v(357.32, -70.87) * mm, "end": v(357.32, -70.67) * mm});
            skLineSegment(sketch, "E533.8", {"start": v(349.6, -40.8) * mm, "end": v(357.6, -40.87) * mm});
            skArc(sketch, "E533.9", {"start": v(698.36, 13.49) * mm, "mid": v(783.56, 4.16) * mm, "end": v(868.97, -2.95) * mm});
            skLineSegment(sketch, "E533.10", {"start": v(695.95, -6.37) * mm, "end": v(698.36, 13.49) * mm});
            skLineSegment(sketch, "E533.11", {"start": v(703.9, -7.33) * mm, "end": v(701.48, -27.19) * mm});
            skLineSegment(sketch, "E533.12", {"start": v(695.95, -6.37) * mm, "end": v(703.9, -7.33) * mm});
            skLineSegment(sketch, "E533.13", {"start": v(701.48, -27.19) * mm, "end": v(868.9, -63.1) * mm});
            skLineSegment(sketch, "E533.14", {"start": v(872.68, -7.2) * mm, "end": v(870.93, -33.16) * mm});
            skLineSegment(sketch, "E533.15", {"start": v(870.93, -33.16) * mm, "end": v(878.9, -33.7) * mm});
            skLineSegment(sketch, "E533.16", {"start": v(878.9, -33.7) * mm, "end": v(880.67, -7.75) * mm});
            skLineSegment(sketch, "E533.17", {"start": v(876.88, -63.63) * mm, "end": v(1043.8, -70.5) * mm});
            skLineSegment(sketch, "E533.18", {"start": v(868.9, -63.1) * mm, "end": v(876.88, -63.63) * mm});
            skLineSegment(sketch, "E533.19", {"start": v(1090.97, -31) * mm, "end": v(1090.97, -51) * mm});
            skLineSegment(sketch, "E533.20", {"start": v(1090.97, -31) * mm, "end": v(1098.97, -31) * mm});
            skLineSegment(sketch, "E533.21", {"start": v(1098.97, -11) * mm, "end": v(1098.97, -31) * mm});
            skLineSegment(sketch, "E534.1", {"start": v(1047.97, -40.66) * mm, "end": v(1055.97, -40.66) * mm});
            skArc(sketch, "E534.3", {"start": v(1003.02, -48.2) * mm, "mid": v(1012.38, -39.58) * mm, "end": v(1003.76, -30.22) * mm});
            skLineSegment(sketch, "E534.4", {"start": v(1003.02, -48.2) * mm, "end": v(923.09, -44.93) * mm});
            skLineSegment(sketch, "E534.5", {"start": v(923.83, -26.95) * mm, "end": v(1003.76, -30.22) * mm});
            skLineSegment(sketch, "E534.6", {"start": v(825.5, -35.65) * mm, "end": v(746.44, -23.43) * mm});
            skArc(sketch, "E534.7", {"start": v(825.5, -35.65) * mm, "mid": v(835.77, -28.13) * mm, "end": v(828.25, -17.86) * mm});
            skLineSegment(sketch, "E534.8", {"start": v(749.2, -5.64) * mm, "end": v(828.25, -17.86) * mm});
            skArc(sketch, "E534.9", {"start": v(746.44, -23.43) * mm, "mid": v(738.92, -13.16) * mm, "end": v(749.2, -5.64) * mm});
            skLineSegment(sketch, "E534.10", {"start": v(220.03, -38.56) * mm, "end": v(299.95, -42.13) * mm});
            skArc(sketch, "E534.11", {"start": v(299.95, -42.13) * mm, "mid": v(309.34, -33.54) * mm, "end": v(300.75, -24.15) * mm});
            skLineSegment(sketch, "E534.12", {"start": v(220.83, -20.58) * mm, "end": v(300.75, -24.15) * mm});
            skArc(sketch, "E534.13", {"start": v(220.03, -38.56) * mm, "mid": v(211.44, -29.17) * mm, "end": v(220.83, -20.58) * mm});
            skLineSegment(sketch, "E534.14", {"start": v(557.8, -20.58) * mm, "end": v(477.88, -24.15) * mm});
            skArc(sketch, "E534.15", {"start": v(478.69, -42.13) * mm, "mid": v(469.3, -33.54) * mm, "end": v(477.88, -24.15) * mm});
            skArc(sketch, "E534.16", {"start": v(558.6, -38.56) * mm, "mid": v(567.2, -29.17) * mm, "end": v(557.8, -20.58) * mm});
            skLineSegment(sketch, "E534.17", {"start": v(558.6, -38.56) * mm, "end": v(478.69, -42.13) * mm});
            skPoint(sketch, "E535.orphan", {"position": v(349.32, -70.8) * mm});
            skLineSegment(sketch, "E536.trimOffspring", {"start": v(357.6, -40.87) * mm, "end": v(357.84, -14.86) * mm});
            skArc(sketch, "E537.trimOffspring", {"start": v(361.87, -10.9) * mm, "mid": v(389.32, -11) * mm, "end": v(416.76, -10.9) * mm});
            skLineSegment(sketch, "E538.MirrorCS", {"start": v(428.79, -14.79) * mm, "end": v(429.03, -40.8) * mm});
            skLineSegment(sketch, "E539.MirrorCS", {"start": v(429.03, -40.8) * mm, "end": v(421.03, -40.87) * mm});
            skLineSegment(sketch, "E540.MirrorCS", {"start": v(421.03, -40.87) * mm, "end": v(420.79, -14.86) * mm});
            skLineSegment(sketch, "E541.MirrorCS", {"start": v(608.98, -44.65) * mm, "end": v(429.32, -70.8) * mm});
            skLineSegment(sketch, "E542.MirrorCS", {"start": v(608.98, -44.65) * mm, "end": v(607.8, -24.68) * mm});
            skLineSegment(sketch, "E543.MirrorCS", {"start": v(614.62, -4.25) * mm, "end": v(615.8, -24.21) * mm});
            skLineSegment(sketch, "E544.MirrorCS", {"start": v(615.8, -24.21) * mm, "end": v(607.8, -24.68) * mm});
            skArc(sketch, "E545.trimOffspring", {"start": v(432.74, -10.75) * mm, "mid": v(523.72, -8.6) * mm, "end": v(614.62, -4.25) * mm});
            skArc(sketch, "E546.trimOffspring", {"start": v(884.92, -4.03) * mm, "mid": v(991.89, -9.26) * mm, "end": v(1098.97, -11) * mm});
            skPoint(sketch, "E547.orphan", {"position": v(1047.97, -70.66) * mm});
            skArc(sketch, "E548.0", {"start": v(349.32, -70.8) * mm, "mid": v(389.32, -71) * mm, "end": v(429.32, -70.8) * mm});
            skArc(sketch, "E549.0", {"start": v(-40, -70.81) * mm, "mid": v(0, -71) * mm, "end": v(40, -70.81) * mm});
            skLineSegment(sketch, "E550.0", {"start": v(1090.97, -51) * mm, "end": v(1083.97, -51) * mm});
            skLineSegment(sketch, "E550.1", {"start": v(1083.97, -51) * mm, "end": v(1083.97, -59) * mm});
            skLineSegment(sketch, "E551.0", {"start": v(1055.97, -40.66) * mm, "end": v(1055.97, -66.66) * mm});
            skLineSegment(sketch, "E551.1", {"start": v(1047.97, -66.5) * mm, "end": v(1047.97, -40.66) * mm});
            skArc(sketch, "E551.2", {"start": v(1043.8, -70.5) * mm, "mid": v(1046.74, -69.38) * mm, "end": v(1047.97, -66.5) * mm});
            skArc(sketch, "E551.3", {"start": v(1055.97, -66.66) * mm, "mid": v(1057.14, -69.5) * mm, "end": v(1059.97, -70.66) * mm});
            skLineSegment(sketch, "E552.0", {"start": v(1059.97, -70.66) * mm, "end": v(1094.97, -70.66) * mm});
            skArc(sketch, "E552.1", {"start": v(1094.97, -70.66) * mm, "mid": v(1097.8, -69.5) * mm, "end": v(1098.97, -66.66) * mm});
            skArc(sketch, "E552.2", {"start": v(1098.97, -63) * mm, "mid": v(1097.8, -60.17) * mm, "end": v(1094.97, -59) * mm});
            skLineSegment(sketch, "E552.4", {"start": v(1098.97, -63) * mm, "end": v(1098.97, -66.66) * mm});
            skPoint(sketch, "E553.visualSharp", {"position": v(880.93, -3.77) * mm});
            skArc(sketch, "E553.filletArc", {"start": v(884.92, -4.03) * mm, "mid": v(882.02, -5) * mm, "end": v(880.67, -7.75) * mm});
            skPoint(sketch, "E554.visualSharp", {"position": v(872.95, -3.23) * mm});
            skArc(sketch, "E554.filletArc", {"start": v(872.68, -7.2) * mm, "mid": v(871.7, -4.31) * mm, "end": v(868.97, -2.95) * mm});
            skPoint(sketch, "E555.visualSharp", {"position": v(349.88, -10.8) * mm});
            skArc(sketch, "E555.filletArc", {"start": v(349.84, -14.79) * mm, "mid": v(348.7, -11.95) * mm, "end": v(345.9, -10.75) * mm});
            skPoint(sketch, "E556.visualSharp", {"position": v(357.88, -10.87) * mm});
            skArc(sketch, "E556.filletArc", {"start": v(361.87, -10.9) * mm, "mid": v(359.04, -12.05) * mm, "end": v(357.84, -14.86) * mm});
            skPoint(sketch, "E557.visualSharp", {"position": v(420.75, -10.87) * mm});
            skArc(sketch, "E557.filletArc", {"start": v(420.79, -14.86) * mm, "mid": v(419.6, -12.05) * mm, "end": v(416.76, -10.9) * mm});
            skPoint(sketch, "E558.visualSharp", {"position": v(428.75, -10.8) * mm});
            skArc(sketch, "E558.filletArc", {"start": v(432.74, -10.75) * mm, "mid": v(429.93, -11.95) * mm, "end": v(428.79, -14.79) * mm});
            skPoint(sketch, "E559.visualSharp", {"position": v(31.49, -10.88) * mm});
            skArc(sketch, "E559.filletArc", {"start": v(31.52, -14.87) * mm, "mid": v(30.33, -12.06) * mm, "end": v(27.5, -10.9) * mm});
            skPoint(sketch, "E560.visualSharp", {"position": v(39.49, -10.81) * mm});
            skArc(sketch, "E560.filletArc", {"start": v(43.48, -10.77) * mm, "mid": v(40.67, -11.97) * mm, "end": v(39.52, -14.8) * mm});
            skPoint(sketch, "E561.visualSharp", {"position": v(-31.49, -10.88) * mm});
            skArc(sketch, "E561.filletArc", {"start": v(-27.5, -10.9) * mm, "mid": v(-30.33, -12.06) * mm, "end": v(-31.52, -14.87) * mm});
            skPoint(sketch, "E562.visualSharp", {"position": v(-39.49, -10.81) * mm});
            skArc(sketch, "E562.filletArc", {"start": v(-39.52, -14.8) * mm, "mid": v(-40.67, -11.97) * mm, "end": v(-43.48, -10.77) * mm});
            skLineSegment(sketch, "E563.0", {"start": v(1083.97, -59) * mm, "end": v(1094.97, -59) * mm});
            skArc(sketch, "E564.0", {"start": v(923.09, -44.93) * mm, "mid": v(914.46, -35.57) * mm, "end": v(923.83, -26.95) * mm});
            skSolve(sketch);
        }
        {
            var Q0;
            Q0=sQuery(id+"F24.wireOp",EDGE,"E447.MirrorCS");
            cPlane(context, id + "F30", {"entities" : qUnion([Q0]), "cplaneType" : CPlaneType.LINE_ANGLE, "offset" : 25 * mm, "angle" : 90 * degree, "width" : 150 * mm, "height" : 150 * mm});
        }
        {
            var Q0;
            Q0=qCreatedBy(id+"F30.planeOp",FACE);
            var sketch = newSketch(context, id + "F31", { "sketchPlane" : qUnion([Q0])});
            skLineSegment(sketch, "E565.0", {"start": v(-1149.97, -70.66) * mm, "end": v(-1149.97, -63.16) * mm});
            skLineSegment(sketch, "E565.6", {"start": v(-1047.97, -70.66) * mm, "end": v(-1047.97, -63.16) * mm});
            skLineSegment(sketch, "E565.7", {"start": v(-1047.97, -70.66) * mm, "end": v(-1149.97, -70.66) * mm});
            skLineSegment(sketch, "E566.0", {"start": v(-1047.97, -63.16) * mm, "end": v(-1055.97, -63.16) * mm});
            skLineSegment(sketch, "E566.1", {"start": v(-1055.97, -55.66) * mm, "end": v(-1055.97, -63.16) * mm});
            skLineSegment(sketch, "E566.2", {"start": v(-1055.97, -55.66) * mm, "end": v(-1141.97, -55) * mm});
            skLineSegment(sketch, "E566.3", {"start": v(-1141.97, -55) * mm, "end": v(-1141.97, -63.16) * mm});
            skLineSegment(sketch, "E566.4", {"start": v(-1149.97, -63.16) * mm, "end": v(-1141.97, -63.16) * mm});
            skSolve(sketch);
        }
        {
            var Q0;
            Q0=qCreatedBy(makeId("Front.planeOp"),FACE);
            var sketch = newSketch(context, id + "F32", { "sketchPlane" : qUnion([Q0])});
            skLineSegment(sketch, "E567.0", {"start": v(1076.44, -5.92) * mm, "end": v(1076.44, -0.5) * mm});
            skLineSegment(sketch, "E567.1", {"start": v(1076.44, -0.5) * mm, "end": v(1094.5, -0.5) * mm});
            skArc(sketch, "E567.2", {"start": v(1094.5, -0.5) * mm, "mid": v(1103.47, 0) * mm, "end": v(1094.5, 0.5) * mm});
            skArc(sketch, "E567.4", {"start": v(1076.44, -5.92) * mm, "mid": v(1087.7, -5.98) * mm, "end": v(1098.97, -6) * mm});
            skLineSegment(sketch, "E567.5", {"start": v(1085.47, 6) * mm, "end": v(1098.97, 6) * mm});
            skLineSegment(sketch, "E567.6", {"start": v(1085.47, 6) * mm, "end": v(1085.47, 0.5) * mm});
            skLineSegment(sketch, "E567.7", {"start": v(1085.47, 0.5) * mm, "end": v(1094.5, 0.5) * mm});
            skArc(sketch, "E568.trimOffspring", {"start": v(1098.97, -6) * mm, "mid": v(1104.97, 0) * mm, "end": v(1098.97, 6) * mm});
            skLineSegment(sketch, "E569.0", {"start": v(375.82, 6) * mm, "end": v(402.82, 6) * mm});
            skLineSegment(sketch, "E569.1", {"start": v(375.82, -5.98) * mm, "end": v(375.82, 6) * mm});
            skArc(sketch, "E569.2", {"start": v(393.79, 0.5) * mm, "mid": v(384.82, 0) * mm, "end": v(393.79, -0.5) * mm});
            skLineSegment(sketch, "E569.3", {"start": v(402.82, 0.5) * mm, "end": v(393.79, 0.5) * mm});
            skLineSegment(sketch, "E569.4", {"start": v(402.82, 6) * mm, "end": v(402.82, 0.5) * mm});
            skLineSegment(sketch, "E569.5", {"start": v(402.82, -0.5) * mm, "end": v(402.82, -5.98) * mm});
            skLineSegment(sketch, "E569.6", {"start": v(402.82, -0.5) * mm, "end": v(393.79, -0.5) * mm});
            skLineSegment(sketch, "E569.7", {"start": v(-13.5, 6) * mm, "end": v(13.5, 6) * mm});
            skLineSegment(sketch, "E569.8", {"start": v(-13.5, -5.98) * mm, "end": v(-13.5, 6) * mm});
            skArc(sketch, "E569.9", {"start": v(4.47, 0.5) * mm, "mid": v(-4.5, 0) * mm, "end": v(4.47, -0.5) * mm});
            skLineSegment(sketch, "E569.10", {"start": v(13.5, 0.5) * mm, "end": v(4.47, 0.5) * mm});
            skLineSegment(sketch, "E569.11", {"start": v(13.5, 6) * mm, "end": v(13.5, 0.5) * mm});
            skLineSegment(sketch, "E569.12", {"start": v(13.5, -0.5) * mm, "end": v(13.5, -5.98) * mm});
            skArc(sketch, "E569.13", {"start": v(-13.5, -5.98) * mm, "mid": v(0, -6) * mm, "end": v(13.5, -5.98) * mm});
            skLineSegment(sketch, "E569.14", {"start": v(13.5, -0.5) * mm, "end": v(4.47, -0.5) * mm});
            skArc(sketch, "E570.0", {"start": v(375.82, -5.98) * mm, "mid": v(389.32, -6) * mm, "end": v(402.82, -5.98) * mm});
            skSolve(sketch);
        }
        {
            var Q0;
            Q0=qCreatedBy(makeId("Front.planeOp"),FACE);
            var sketch = newSketch(context, id + "F33", { "sketchPlane" : qUnion([Q0])});
            skPoint(sketch, "E571.0", {"position": v(0, 0) * mm});
            skPoint(sketch, "E571.1", {"position": v(389.32, 0) * mm});
            skPoint(sketch, "E571.2", {"position": v(1098.97, 0) * mm});
            skArc(sketch, "E572", {"start": v(-46.06, -54.04) * mm, "mid": v(-1.52, -70.99) * mm, "end": v(43.7, -55.97) * mm});
            skCircle(sketch, "E573", {"center": v(0, 100) * mm, "radius": 3 * mm});
            skArc(sketch, "E574", {"start": v(-4.83, 101.28) * mm, "mid": v(0.04, 105) * mm, "end": v(4.85, 101.2) * mm});
            skLineSegment(sketch, "E575", {"start": v(-4.83, 101.28) * mm, "end": v(-46.06, -54.04) * mm});
            skLineSegment(sketch, "E576", {"start": v(4.85, 101.2) * mm, "end": v(43.7, -55.97) * mm});
            skArc(sketch, "E577", {"start": v(-44.33, -47.54) * mm, "mid": v(-1.5, -64.98) * mm, "end": v(42.1, -49.52) * mm, "construction": true});
            skLineSegment(sketch, "E578", {"start": v(0, 0) * mm, "end": v(-26.42, -59.39) * mm, "construction": true});
            skLineSegment(sketch, "E579", {"start": v(-43.7, -55.97) * mm, "end": v(0, 0) * mm, "construction": true});
            skLineSegment(sketch, "E580", {"start": v(0, 0) * mm, "end": v(0, -71) * mm, "construction": true});
            skLineSegment(sketch, "E581", {"start": v(0, 0) * mm, "end": v(43.7, -55.97) * mm, "construction": true});
            skLineSegment(sketch, "E582", {"start": v(0, 100) * mm, "end": v(0, 66.67) * mm, "construction": true});
            skLineSegment(sketch, "E583", {"start": v(0, 66.67) * mm, "end": v(0, 33.33) * mm, "construction": true});
            skLineSegment(sketch, "E584", {"start": v(0, 33.33) * mm, "end": v(0, 0) * mm, "construction": true});
            skCircle(sketch, "E585", {"center": v(0, 66.67) * mm, "radius": 3 * mm});
            skCircle(sketch, "E586.1", {"center": v(0, 0) * mm, "radius": 3 * mm});
            skArc(sketch, "E587", {"start": v(-41.23, -52.81) * mm, "mid": v(-41.58, -50) * mm, "end": v(-38.77, -49.66) * mm});
            skArc(sketch, "E588", {"start": v(-25.6, -57.56) * mm, "mid": v(-24.59, -60.2) * mm, "end": v(-27.23, -61.22) * mm});
            skArc(sketch, "E589", {"start": v(-38.77, -49.66) * mm, "mid": v(-32.43, -54.01) * mm, "end": v(-25.6, -57.56) * mm});
            skArc(sketch, "E590", {"start": v(-41.23, -52.81) * mm, "mid": v(-34.49, -57.44) * mm, "end": v(-27.23, -61.22) * mm});
            skLineSegment(sketch, "E591", {"start": v(0, 0) * mm, "end": v(-20.06, -61.83) * mm, "construction": true});
            skArc(sketch, "E592.MirrorCS", {"start": v(-13.08, -61.63) * mm, "mid": v(-15.45, -63.17) * mm, "end": v(-13.9, -65.54) * mm});
            skArc(sketch, "E593.MirrorCS", {"start": v(2.22, -62.96) * mm, "mid": v(-5.47, -62.76) * mm, "end": v(-13.08, -61.63) * mm});
            skArc(sketch, "E594.MirrorCS", {"start": v(2.36, -66.96) * mm, "mid": v(-5.82, -66.75) * mm, "end": v(-13.9, -65.54) * mm});
            skArc(sketch, "E595.MirrorCS", {"start": v(2.36, -66.96) * mm, "mid": v(4.3, -64.89) * mm, "end": v(2.22, -62.96) * mm});
            skLineSegment(sketch, "E596.MirrorCS", {"start": v(0, 0) * mm, "end": v(-13.5, -63.58) * mm, "construction": true});
            skLineSegment(sketch, "E597.MirrorCS", {"start": v(2.5, -70.96) * mm, "end": v(0, 0) * mm, "construction": true});
            skLineSegment(sketch, "E598", {"start": v(0, 0) * mm, "end": v(9.07, -64.36) * mm, "construction": true});
            skLineSegment(sketch, "E599.MirrorCS", {"start": v(17.2, -68.89) * mm, "end": v(0, 0) * mm, "construction": true});
            skArc(sketch, "E600.MirrorCS", {"start": v(16.23, -65) * mm, "mid": v(13.8, -63.55) * mm, "end": v(15.26, -61.12) * mm});
            skArc(sketch, "E601.MirrorCS", {"start": v(15.26, -61.12) * mm, "mid": v(22.6, -58.8) * mm, "end": v(29.6, -55.62) * mm});
            skArc(sketch, "E602.MirrorCS", {"start": v(29.6, -55.62) * mm, "mid": v(32.3, -56.44) * mm, "end": v(31.48, -59.15) * mm});
            skArc(sketch, "E603.MirrorCS", {"start": v(16.23, -65) * mm, "mid": v(24.03, -62.54) * mm, "end": v(31.48, -59.15) * mm});
            skArc(sketch, "E604.0", {"start": v(-40, -70.81) * mm, "mid": v(0, -71) * mm, "end": v(40, -70.81) * mm, "construction": true});
            skCircle(sketch, "E605.1.0.0", {"center": v(389.32, 0) * mm, "radius": 3 * mm});
            skLineSegment(sketch, "E605.1.0.1", {"start": v(384.48, 101.28) * mm, "end": v(343.26, -54.04) * mm});
            skLineSegment(sketch, "E605.1.0.2", {"start": v(394.17, 101.2) * mm, "end": v(433, -55.97) * mm});
            skArc(sketch, "E605.1.0.3", {"start": v(343.26, -54.04) * mm, "mid": v(387.8, -70.99) * mm, "end": v(433, -55.97) * mm});
            skArc(sketch, "E605.1.0.4", {"start": v(348.09, -52.81) * mm, "mid": v(354.83, -57.44) * mm, "end": v(362.09, -61.22) * mm});
            skArc(sketch, "E605.1.0.5", {"start": v(350.55, -49.66) * mm, "mid": v(356.89, -54.01) * mm, "end": v(363.71, -57.56) * mm});
            skArc(sketch, "E605.1.0.6", {"start": v(348.09, -52.81) * mm, "mid": v(347.74, -50) * mm, "end": v(350.55, -49.66) * mm});
            skArc(sketch, "E605.1.0.7", {"start": v(363.71, -57.56) * mm, "mid": v(364.73, -60.2) * mm, "end": v(362.09, -61.22) * mm});
            skArc(sketch, "E605.1.0.8", {"start": v(391.54, -62.96) * mm, "mid": v(383.85, -62.76) * mm, "end": v(376.24, -61.63) * mm});
            skArc(sketch, "E605.1.0.9", {"start": v(376.24, -61.63) * mm, "mid": v(373.87, -63.17) * mm, "end": v(375.4, -65.54) * mm});
            skArc(sketch, "E605.1.0.10", {"start": v(391.68, -66.96) * mm, "mid": v(383.5, -66.75) * mm, "end": v(375.4, -65.54) * mm});
            skArc(sketch, "E605.1.0.11", {"start": v(391.68, -66.96) * mm, "mid": v(393.6, -64.89) * mm, "end": v(391.54, -62.96) * mm});
            skArc(sketch, "E605.1.0.12", {"start": v(405.55, -65) * mm, "mid": v(403.12, -63.55) * mm, "end": v(404.58, -61.12) * mm});
            skArc(sketch, "E605.1.0.13", {"start": v(405.55, -65) * mm, "mid": v(413.35, -62.54) * mm, "end": v(420.8, -59.15) * mm});
            skArc(sketch, "E605.1.0.14", {"start": v(404.58, -61.12) * mm, "mid": v(411.91, -58.8) * mm, "end": v(418.91, -55.62) * mm});
            skArc(sketch, "E605.1.0.15", {"start": v(418.91, -55.62) * mm, "mid": v(421.62, -56.44) * mm, "end": v(420.8, -59.15) * mm});
            skCircle(sketch, "E605.1.0.16", {"center": v(389.32, 66.67) * mm, "radius": 3 * mm});
            skCircle(sketch, "E605.1.0.17", {"center": v(389.32, 100) * mm, "radius": 3 * mm});
            skArc(sketch, "E605.1.0.18", {"start": v(384.48, 101.28) * mm, "mid": v(389.36, 105) * mm, "end": v(394.17, 101.2) * mm});
            skLineSegment(sketch, "E605.direction1", {"start": v(0, 0) * mm, "end": v(389.32, 0) * mm, "construction": true});
            skCircle(sketch, "E606.1.0.0", {"center": v(1098.97, 0) * mm, "radius": 3 * mm});
            skArc(sketch, "E606.1.0.1", {"start": v(1057.74, -52.81) * mm, "mid": v(1064.48, -57.44) * mm, "end": v(1071.74, -61.22) * mm});
            skLineSegment(sketch, "E606.1.0.2", {"start": v(1094.14, 101.28) * mm, "end": v(1052.91, -54.04) * mm});
            skArc(sketch, "E606.1.0.3", {"start": v(1101.2, -62.96) * mm, "mid": v(1093.5, -62.76) * mm, "end": v(1085.9, -61.63) * mm});
            skArc(sketch, "E606.1.0.5", {"start": v(1114.23, -61.12) * mm, "mid": v(1121.57, -58.8) * mm, "end": v(1128.57, -55.62) * mm});
            skArc(sketch, "E606.1.0.6", {"start": v(1060.2, -49.66) * mm, "mid": v(1066.54, -54.01) * mm, "end": v(1073.37, -57.56) * mm});
            skArc(sketch, "E606.1.0.7", {"start": v(1115.2, -65) * mm, "mid": v(1123, -62.54) * mm, "end": v(1130.45, -59.15) * mm});
            skArc(sketch, "E606.1.0.8", {"start": v(1101.33, -66.96) * mm, "mid": v(1093.15, -66.75) * mm, "end": v(1085.06, -65.54) * mm});
            skArc(sketch, "E606.1.0.9", {"start": v(1094.14, 101.28) * mm, "mid": v(1099.01, 105) * mm, "end": v(1103.82, 101.2) * mm});
            skLineSegment(sketch, "E606.1.0.10", {"start": v(1103.82, 101.2) * mm, "end": v(1142.66, -55.97) * mm});
            skArc(sketch, "E606.1.0.11", {"start": v(1052.91, -54.04) * mm, "mid": v(1097.45, -70.99) * mm, "end": v(1142.66, -55.97) * mm});
            skCircle(sketch, "E606.1.0.12", {"center": v(1098.97, 66.67) * mm, "radius": 3 * mm});
            skArc(sketch, "E606.1.0.13", {"start": v(1101.33, -66.96) * mm, "mid": v(1103.26, -64.89) * mm, "end": v(1101.2, -62.96) * mm});
            skArc(sketch, "E606.1.0.14", {"start": v(1073.37, -57.56) * mm, "mid": v(1074.38, -60.2) * mm, "end": v(1071.74, -61.22) * mm});
            skCircle(sketch, "E606.1.0.15", {"center": v(1098.97, 100) * mm, "radius": 3 * mm});
            skArc(sketch, "E606.1.0.16", {"start": v(1057.74, -52.81) * mm, "mid": v(1057.4, -50) * mm, "end": v(1060.2, -49.66) * mm});
            skArc(sketch, "E606.1.0.17", {"start": v(1115.2, -65) * mm, "mid": v(1112.78, -63.55) * mm, "end": v(1114.23, -61.12) * mm});
            skArc(sketch, "E606.1.0.18", {"start": v(1128.57, -55.62) * mm, "mid": v(1131.27, -56.44) * mm, "end": v(1130.45, -59.15) * mm});
            skArc(sketch, "E606.1.0.19", {"start": v(1085.9, -61.63) * mm, "mid": v(1083.52, -63.17) * mm, "end": v(1085.06, -65.54) * mm});
            skLineSegment(sketch, "E606.direction1", {"start": v(389.32, 0) * mm, "end": v(1098.97, 0) * mm, "construction": true});
            skLineSegment(sketch, "E607", {"start": v(-44.33, -47.54) * mm, "end": v(0, 0) * mm, "construction": true});
            skSolve(sketch);
        }
        {
            var Q0;
            Q0=sQuery(id+"F13.wireOp",VERTEX,"E358.end");
            var Q1;
            Q1=qCreatedBy(makeId("Front.planeOp"),FACE);
            cPlane(context, id + "F34", {"entities" : qUnion([Q0, Q1]), "cplaneType" : CPlaneType.PLANE_POINT, "offset" : 25 * mm, "width" : 150 * mm, "height" : 150 * mm});
        }
        {
            var Q0;
            Q0=qCreatedBy(makeId("Right.planeOp"),FACE);
            var Q1;
            Q1=sQuery(id+"F9.wireOp",VERTEX,"E136.center");
            cPlane(context, id + "F35", {"entities" : qUnion([Q0, Q1]), "cplaneType" : CPlaneType.PLANE_POINT, "offset" : 25 * mm, "width" : 150 * mm, "height" : 150 * mm});
        }
        {
            var Q0;
            Q0=sQuery(id+"F9.wireOp",VERTEX,"E174");
            var Q1;
            Q1=qCreatedBy(makeId("Right.planeOp"),FACE);
            cPlane(context, id + "F36", {"entities" : qUnion([Q0, Q1]), "cplaneType" : CPlaneType.PLANE_POINT, "offset" : 25 * mm, "width" : 150 * mm, "height" : 150 * mm});
        }
        {
            var Q0;
            Q0 = qSketchRegion(id + "F10", true);
            var Q1;
            Q1 = qSketchRegion(id + "F29", true);
            var Q2;
            Q2 = qSketchRegion(id + "F31", true);
            extrude(context, id + "F37", {"entities" : qUnion([Q0, Q1, Q2]), "depth" : (getVariable(context, 'ePlaque')) * mm});
        }
        {
            var Q0;
            Q0 = qSketchRegion(id + "F13", true);
            var Q1;
            Q1 = qSketchRegion(id + "F17", true);
            var Q2;
            Q2 = qSketchRegion(id + "F19", true);
            var Q3;
            Q3 = qSketchRegion(id + "F15", true);
            var Q4;
            Q4 = qSketchRegion(id + "F25", true);
            var Q5;
            Q5 = qSketchRegion(id + "F26", true);
            var Q6;
            Q6 = qSketchRegion(id + "F24", true);
            extrude(context, id + "F38", {"entities" : qUnion([Q0, Q1, Q2, Q3, Q4, Q5, Q6]), "endBound" : BoundingType.SYMMETRIC, "depth" : (getVariable(context, 'ePlaque')) * mm});
        }
        {
            var Q0;
            Q0 = qSketchRegion(id + "F27", true);
            extrude(context, id + "F39", {"entities" : qUnion([Q0]), "depth" : (getVariable(context, 'ePlaque')) * mm});
        }
        {
            var Q0;
            {var subQ7=sQuery(id+"F9.wireOp",EDGE,"E121");Q0=makeQuery(id+"F9.imprint","IMPRINT",FACE,{"disambiguationData":[TD([[makeQuery(id+"F9.imprint","IMPRINT",EDGE,{"derivedFrom":subQ7}),1.0]])]});}
            var Q1;
            {var subQ5=sQuery(id+"F9.wireOp",EDGE,"E113");Q1=makeQuery(id+"F9.imprint","IMPRINT",FACE,{"disambiguationData":[TD([[makeQuery(id+"F9.imprint","IMPRINT",EDGE,{"derivedFrom":subQ5}),-1.0]])]});}
            var Q2;
            {var subQ5=sQuery(id+"F9.wireOp",EDGE,"E147");Q2=makeQuery(id+"F9.imprint","IMPRINT",FACE,{"disambiguationData":[TD([[makeQuery(id+"F9.imprint","IMPRINT",EDGE,{"derivedFrom":subQ5}),-1.0]])]});}
            var Q3;
            {var subQ8=sQuery(id+"F9.wireOp",EDGE,"E140");Q3=makeQuery(id+"F9.imprint","IMPRINT",FACE,{"disambiguationData":[TD([[makeQuery(id+"F9.imprint","IMPRINT",EDGE,{"derivedFrom":subQ8}),1.0]])]});}
            var Q4;
            {var subQ1=sQuery(id+"F9.wireOp",EDGE,"E178");Q4=makeQuery(id+"F9.imprint","IMPRINT",FACE,{"disambiguationData":[TD([[makeQuery(id+"F9.imprint","IMPRINT",EDGE,{"derivedFrom":subQ1}),1.0]])]});}
            var Q5;
            Q5=makeQuery(id+"F9.imprint","IMPRINT",FACE,{"disambiguationData":[TD([[makeQuery(id+"F9.imprint","IMPRINT",EDGE,{"derivedFrom":sQuery(id+"F9.wireOp",EDGE,"E202.bottom")}),1.0]])]});
            var Q6;
            {var subQ1=sQuery(id+"F9.wireOp",EDGE,"E155.left");Q6=makeQuery(id+"F9.imprint","IMPRINT",FACE,{"disambiguationData":[TD([[makeQuery(id+"F9.imprint","IMPRINT",EDGE,{"derivedFrom":subQ1}),1.0]])]});}
            var Q7;
            {var subQ6=sQuery(id+"F9.wireOp",EDGE,"E129.left");Q7=makeQuery(id+"F9.imprint","IMPRINT",FACE,{"disambiguationData":[TD([[makeQuery(id+"F9.imprint","IMPRINT",EDGE,{"derivedFrom":subQ6}),1.0]])]});}
            extrude(context, id + "F40", {"entities" : qUnion([Q0, Q1, Q2, Q3, Q4, Q5, Q6, Q7]), "depth" : (getVariable(context, 'lFacette')) * mm});
        }
        {
            var Q0;
            Q0 = qSketchRegion(id + "F32", true);
            extrude(context, id + "F41", {"entities" : qUnion([Q0]), "operationType" : NewBodyOperationType.ADD, "depth" : (getVariable(context, 'ePlaque')) * mm});
        }
        {
            var Q0;
            Q0=makeQuery(id+"F11.imprint","IMPRINT",FACE,{"disambiguationData":[TD([[makeQuery(id+"F11.imprint","IMPRINT",EDGE,{"derivedFrom":sQuery(id+"F11.wireOp",EDGE,"E336")}),-1.0]])]});
            var Q1;
            {var subQ0=sQuery(id+"F11.wireOp",EDGE,"E343");Q1=makeQuery(id+"F11.imprint","IMPRINT",FACE,{"disambiguationData":[TD([[makeQuery(id+"F11.imprint","IMPRINT",EDGE,{"derivedFrom":subQ0}),1.0]])]});}
            var Q2;
            Q2=makeQuery(id+"F11.imprint","IMPRINT",FACE,{"disambiguationData":[TD([[makeQuery(id+"F11.imprint","IMPRINT",EDGE,{"derivedFrom":sQuery(id+"F11.wireOp",EDGE,"E339.MirrorC")}),1.0]])]});
            extrude(context, id + "F42", {"entities" : qUnion([Q0, Q1, Q2]), "oppositeDirection" : true, "depth" : (getVariable(context, 'ePlaque')) * mm});
        }
        {
            var Q0;
            Q0=makeQuery(id+"F11.imprint","IMPRINT",FACE,{"disambiguationData":[TD([[makeQuery(id+"F11.imprint","IMPRINT",EDGE,{"derivedFrom":sQuery(id+"F11.wireOp",EDGE,"E336")}),-1.0]])]});
            var Q1;
            Q1=makeQuery(id+"F11.imprint","IMPRINT",FACE,{"disambiguationData":[TD([[makeQuery(id+"F11.imprint","IMPRINT",EDGE,{"derivedFrom":sQuery(id+"F11.wireOp",EDGE,"E339.MirrorC")}),1.0]])]});
            var Q2;
            {var subQ0=sQuery(id+"F11.wireOp",EDGE,"E350.MirrorCS");Q2=makeQuery(id+"F11.imprint","IMPRINT",FACE,{"disambiguationData":[TD([[makeQuery(id+"F11.imprint","IMPRINT",EDGE,{"derivedFrom":subQ0}),-1.0]])]});}
            extrude(context, id + "F43", {"entities" : qUnion([Q0, Q1, Q2]), "operationType" : NewBodyOperationType.ADD, "oppositeDirection" : true, "depth" : (2 * getVariable(context, 'ePlaque')) * mm, "hasSecondDirection" : true, "secondDirectionOppositeDirection" : true, "secondDirectionDepth" : (getVariable(context, 'ePlaque')) * mm});
        }
        {
            var Q0;
            Q0 = qSketchRegion(id + "F33", true);
            extrude(context, id + "F44", {"entities" : qUnion([Q0]), "oppositeDirection" : true, "depth" : 0.8 * mm});
        }
        {
            var Q0;
            {var subQ0=sQuery(id+"F11.wireOp",EDGE,"E344.MirrorCS");Q0=makeQuery(id+"F11.imprint","IMPRINT",FACE,{"disambiguationData":[TD([[makeQuery(id+"F11.imprint","IMPRINT",EDGE,{"derivedFrom":subQ0}),1.0]])]});}
            var Q1;
            {var subQ0=sQuery(id+"F11.wireOp",EDGE,"E350.MirrorCS");Q1=makeQuery(id+"F11.imprint","IMPRINT",FACE,{"disambiguationData":[TD([[makeQuery(id+"F11.imprint","IMPRINT",EDGE,{"derivedFrom":subQ0}),-1.0]])]});}
            extrude(context, id + "F45", {"entities" : qUnion([Q0, Q1]), "oppositeDirection" : true, "depth" : (getVariable(context, 'ePlaque')) * mm});
        }
        {
            var Q0;
            {var subQ0=sQuery(id+"F11.wireOp",EDGE,"E344.MirrorCS");Q0=makeQuery(id+"F11.imprint","IMPRINT",FACE,{"disambiguationData":[TD([[makeQuery(id+"F11.imprint","IMPRINT",EDGE,{"derivedFrom":subQ0}),1.0]])]});}
            var Q1;
            {var subQ0=sQuery(id+"F11.wireOp",EDGE,"E343");Q1=makeQuery(id+"F11.imprint","IMPRINT",FACE,{"disambiguationData":[TD([[makeQuery(id+"F11.imprint","IMPRINT",EDGE,{"derivedFrom":subQ0}),1.0]])]});}
            extrude(context, id + "F46", {"entities" : qUnion([Q0, Q1]), "operationType" : NewBodyOperationType.ADD, "oppositeDirection" : true, "depth" : (2 * getVariable(context, 'ePlaque')) * mm, "hasSecondDirection" : true, "secondDirectionOppositeDirection" : true, "secondDirectionDepth" : (getVariable(context, 'ePlaque')) * mm});
        }
        {
            var Q0;
            Q0=makeQuery(id+"F38.opExtrude","SWEPT_BODY",BODY,{"disambiguationData":[OSD([sQuery(id+"F15.wireOp",EDGE,"E373"),sQuery(id+"F15.wireOp",EDGE,"mjyUZ6ak-vkji-SJxo-2XNz-AzQJBSIhJCq7"),sQuery(id+"F15.wireOp",EDGE,"E374"),sQuery(id+"F15.wireOp",EDGE,"V8wbWLWV-mXVU-s5Be-ogwu-GwHMpDDGAR26"),sQuery(id+"F15.wireOp",EDGE,"Aa746kcm-iTco-Hja0-MqTk-uI1FuPpx7sIC"),sQuery(id+"F15.wireOp",EDGE,"0gMpWZH2-X4Bq-B8Kj-kDG7-pci8WuajTVCi"),sQuery(id+"F15.wireOp",EDGE,"DgVHAKVQ-NtFD-0pMv-gzqq-eGHJCLSba262"),sQuery(id+"F15.wireOp",EDGE,"7d46042e-4088-480c-827d-0d95e9e3ada70.MirrorCS"),sQuery(id+"F15.wireOp",EDGE,"992acb48-d8e6-4953-9221-bb7522425a2a0.MirrorCS"),sQuery(id+"F15.wireOp",EDGE,"30251e60-abcf-41ef-bc21-ea780fc9dcf10.MirrorCS"),sQuery(id+"F15.wireOp",EDGE,"24bb8814-cb35-4dc2-b604-5638a420d6f80.MirrorCS"),sQuery(id+"F15.wireOp",EDGE,"b9d52511-03c4-42c3-bf58-efa4341616910.MirrorCS"),sQuery(id+"F15.wireOp",EDGE,"E377.MirrorCS"),sQuery(id+"F15.wireOp",EDGE,"c9f2f1c8-64f3-4b4f-ba4c-64e3ef61d2b50.MirrorCS"),sQuery(id+"F15.wireOp",EDGE,"E378"),sQuery(id+"F15.wireOp",EDGE,"VMgRDk3k-e7VJ-ArGT-NcPX-NCIs0FO0DYiq")])]});
            var Q1;
            Q1=makeQuery(id+"F38.opExtrude","SWEPT_BODY",BODY,{"disambiguationData":[OSD([sQuery(id+"F13.wireOp",EDGE,"soK8HYBu-wfng-zAhJ-nHhD-1IelcYUYImG8.bottom"),sQuery(id+"F13.wireOp",EDGE,"E354"),sQuery(id+"F13.wireOp",EDGE,"E355"),sQuery(id+"F13.wireOp",EDGE,"E356"),sQuery(id+"F13.wireOp",EDGE,"E357"),sQuery(id+"F13.wireOp",EDGE,"EzmpK47F-kDqr-Wh7p-gqRm-WuETrRyEMbgO"),sQuery(id+"F13.wireOp",EDGE,"E359"),sQuery(id+"F13.wireOp",EDGE,"u4PaVtaW-PCwE-sbOI-MS99-ZI9KKZLca25e"),sQuery(id+"F13.wireOp",EDGE,"c0fa8e0a-a987-414d-ab34-8595a56f63fc.trimOffspring"),sQuery(id+"F13.wireOp",EDGE,"E360.MirrorCS"),sQuery(id+"F13.wireOp",EDGE,"f0c5c619-b336-441d-9e60-c776ea3468b71.MirrorCS"),sQuery(id+"F13.wireOp",EDGE,"f0c5c619-b336-441d-9e60-c776ea3468b72.MirrorCS"),sQuery(id+"F13.wireOp",EDGE,"E361.MirrorCS"),sQuery(id+"F13.wireOp",EDGE,"E362.MirrorCS"),sQuery(id+"F13.wireOp",EDGE,"E363.MirrorCS"),sQuery(id+"F13.wireOp",EDGE,"8b1bb375-89ab-4616-944a-9adde5556f26.trimOffspring")])]});
            var Q2;
            Q2=qCreatedBy(makeId("Right.planeOp"),FACE);
            mirror(context, id + "F47", {"entities" : qUnion([Q0, Q1]), "mirrorPlane" : qUnion([Q2])});
        }
        {
            var Q0;
            Q0=makeQuery(id+"F38.opExtrude","SWEPT_BODY",BODY,{"disambiguationData":[OSD([sQuery(id+"F17.wireOp",EDGE,"E395"),sQuery(id+"F17.wireOp",EDGE,"E396"),sQuery(id+"F17.wireOp",EDGE,"E397"),sQuery(id+"F17.wireOp",EDGE,"E398.MirrorCS"),sQuery(id+"F17.wireOp",EDGE,"E399.MirrorCS"),sQuery(id+"F17.wireOp",EDGE,"E400.MirrorCS"),sQuery(id+"F17.wireOp",EDGE,"E401"),sQuery(id+"F17.wireOp",EDGE,"Q4O6iqY6-R77D-6AVI-t65V-7jzikAPxFFEY"),sQuery(id+"F17.wireOp",EDGE,"nMmm8wN5-3bnS-mXfy-erN5-3AUfeU6LnbjA"),sQuery(id+"F17.wireOp",EDGE,"sj0Nv4Aq-dxry-ov99-KMoX-cL0KEdvW9e3V"),sQuery(id+"F17.wireOp",EDGE,"E402"),sQuery(id+"F17.wireOp",EDGE,"f9ee0f4f-ba50-4059-9d26-70d4bc067ac90.MirrorCS"),sQuery(id+"F17.wireOp",EDGE,"e94ccbfd-ac80-4812-8ae6-408e85db5e050.MirrorCS"),sQuery(id+"F17.wireOp",EDGE,"09305a33-f280-46ca-a3d2-4531643ebfd90.MirrorCS"),sQuery(id+"F17.wireOp",EDGE,"889ecba0-25f8-4a03-bf02-64d85be8d6480.MirrorCS"),sQuery(id+"F17.wireOp",EDGE,"TjOl2SVP-R3db-IKb3-KQe8-QRhjwxNyGWqU")])]});
            var Q1;
            Q1=makeQuery(id+"F38.opExtrude","SWEPT_BODY",BODY,{"disambiguationData":[OSD([sQuery(id+"F19.wireOp",EDGE,"4YzY6mux-AE96-hHzq-ig6u-TRBUy3hHa8ce"),sQuery(id+"F19.wireOp",EDGE,"E413"),sQuery(id+"F19.wireOp",EDGE,"u9lkLUbf-7qaw-ysuW-smsC-FF3ijep48Epg"),sQuery(id+"F19.wireOp",EDGE,"E414"),sQuery(id+"F19.wireOp",EDGE,"5kOxIgGm-yVoc-yF6B-4yi4-uPNAgYRws7i0"),sQuery(id+"F19.wireOp",EDGE,"kuHAFuTL-Kc1G-Rmqk-xmvD-0N2kUWLfF7Dw"),sQuery(id+"F19.wireOp",EDGE,"qLdkrune-M0s0-iYU3-dQh0-0YBpp6H5zhtL"),sQuery(id+"F19.wireOp",EDGE,"5b090ae0-e64e-4648-9bb9-968468e266ba0.MirrorCS"),sQuery(id+"F19.wireOp",EDGE,"46527eb5-82b1-4274-83e7-e87fc75ffadf0.MirrorCS"),sQuery(id+"F19.wireOp",EDGE,"6f8005dc-c516-42e9-a0f7-32f03c0f1b600.MirrorCS"),sQuery(id+"F19.wireOp",EDGE,"d2b16510-180e-4b2f-9a33-6f0c5e87fbe90.MirrorCS"),sQuery(id+"F19.wireOp",EDGE,"561eb118-1a3c-45ae-a9b5-88ebef0dc23a0.MirrorCS"),sQuery(id+"F19.wireOp",EDGE,"E415.MirrorCS"),sQuery(id+"F19.wireOp",EDGE,"27570078-b251-4886-a000-94cb742776480.MirrorCS"),sQuery(id+"F19.wireOp",EDGE,"wrZN9VGC-SinS-Khfq-DM0g-TTBQbXDlLIrs"),sQuery(id+"F19.wireOp",EDGE,"YtZUYQK4-TOJb-Pmlt-oqoi-kuRJWNaoSKdf")])]});
            var Q2;
            Q2=qCreatedBy(id+"F35.planeOp",FACE);
            mirror(context, id + "F48", {"entities" : qUnion([Q0, Q1]), "mirrorPlane" : qUnion([Q2])});
        }
        {
            var Q0;
            Q0=makeQuery(id+"F37.opExtrude","SWEPT_BODY",BODY,{"disambiguationData":[OSD([sQuery(id+"F10.wireOp",EDGE,"E294.0"),sQuery(id+"F10.wireOp",EDGE,"E294.1"),sQuery(id+"F10.wireOp",EDGE,"E294.2"),sQuery(id+"F10.wireOp",EDGE,"E294.3"),sQuery(id+"F10.wireOp",EDGE,"E294.4"),sQuery(id+"F10.wireOp",EDGE,"E294.5"),sQuery(id+"F10.wireOp",EDGE,"E294.6"),sQuery(id+"F10.wireOp",EDGE,"E294.7"),sQuery(id+"F10.wireOp",EDGE,"E294.8"),sQuery(id+"F10.wireOp",EDGE,"E294.9"),sQuery(id+"F10.wireOp",EDGE,"E294.10"),sQuery(id+"F10.wireOp",EDGE,"E294.11"),sQuery(id+"F10.wireOp",EDGE,"E294.12"),sQuery(id+"F10.wireOp",EDGE,"E294.14"),sQuery(id+"F10.wireOp",EDGE,"E300"),sQuery(id+"F10.wireOp",EDGE,"E301"),sQuery(id+"F10.wireOp",EDGE,"E302"),sQuery(id+"F10.wireOp",EDGE,"E303"),sQuery(id+"F10.wireOp",EDGE,"E309"),sQuery(id+"F10.wireOp",EDGE,"E310"),sQuery(id+"F10.wireOp",EDGE,"E311"),sQuery(id+"F10.wireOp",EDGE,"E312"),sQuery(id+"F10.wireOp",EDGE,"E313.0"),sQuery(id+"F10.wireOp",EDGE,"E313.1"),sQuery(id+"F10.wireOp",EDGE,"E313.2"),sQuery(id+"F10.wireOp",EDGE,"E316.0"),sQuery(id+"F10.wireOp",EDGE,"E316.1"),sQuery(id+"F10.wireOp",EDGE,"E316.2"),sQuery(id+"F10.wireOp",EDGE,"E316.4"),sQuery(id+"F10.wireOp",EDGE,"E325.filletArc"),sQuery(id+"F10.wireOp",EDGE,"E326.filletArc"),sQuery(id+"F10.wireOp",EDGE,"E327.filletArc"),sQuery(id+"F10.wireOp",EDGE,"E328.filletArc"),sQuery(id+"F10.wireOp",EDGE,"E329.filletArc"),sQuery(id+"F10.wireOp",EDGE,"E330.filletArc"),sQuery(id+"F10.wireOp",EDGE,"E331.filletArc"),sQuery(id+"F10.wireOp",EDGE,"E332.0")])]});
            var Q1;
            Q1=makeQuery(id+"F37.opExtrude","SWEPT_BODY",BODY,{"disambiguationData":[OSD([sQuery(id+"F29.wireOp",EDGE,"E533.9"),sQuery(id+"F29.wireOp",EDGE,"E533.10"),sQuery(id+"F29.wireOp",EDGE,"E533.11"),sQuery(id+"F29.wireOp",EDGE,"E533.12"),sQuery(id+"F29.wireOp",EDGE,"E533.13"),sQuery(id+"F29.wireOp",EDGE,"E533.14"),sQuery(id+"F29.wireOp",EDGE,"E533.15"),sQuery(id+"F29.wireOp",EDGE,"E533.16"),sQuery(id+"F29.wireOp",EDGE,"E533.17"),sQuery(id+"F29.wireOp",EDGE,"E533.18"),sQuery(id+"F29.wireOp",EDGE,"E533.19"),sQuery(id+"F29.wireOp",EDGE,"E533.20"),sQuery(id+"F29.wireOp",EDGE,"E533.21"),sQuery(id+"F29.wireOp",EDGE,"E534.1"),sQuery(id+"F29.wireOp",EDGE,"E534.6"),sQuery(id+"F29.wireOp",EDGE,"E534.7"),sQuery(id+"F29.wireOp",EDGE,"E534.8"),sQuery(id+"F29.wireOp",EDGE,"E534.9"),sQuery(id+"F29.wireOp",EDGE,"E546.trimOffspring"),sQuery(id+"F29.wireOp",EDGE,"E550.0"),sQuery(id+"F29.wireOp",EDGE,"E550.1"),sQuery(id+"F29.wireOp",EDGE,"E551.0"),sQuery(id+"F29.wireOp",EDGE,"E551.1"),sQuery(id+"F29.wireOp",EDGE,"E551.2"),sQuery(id+"F29.wireOp",EDGE,"E551.3"),sQuery(id+"F29.wireOp",EDGE,"E552.0"),sQuery(id+"F29.wireOp",EDGE,"E552.1"),sQuery(id+"F29.wireOp",EDGE,"E552.2"),sQuery(id+"F29.wireOp",EDGE,"E552.4"),sQuery(id+"F29.wireOp",EDGE,"E553.filletArc"),sQuery(id+"F29.wireOp",EDGE,"E554.filletArc"),sQuery(id+"F29.wireOp",EDGE,"E563.0")])]});
            var Q2;
            Q2=makeQuery(id+"F37.opExtrude","SWEPT_BODY",BODY,{"disambiguationData":[OSD([sQuery(id+"F29.wireOp",EDGE,"E533.0"),sQuery(id+"F29.wireOp",EDGE,"E533.1"),sQuery(id+"F29.wireOp",EDGE,"E533.2"),sQuery(id+"F29.wireOp",EDGE,"E533.3"),sQuery(id+"F29.wireOp",EDGE,"E533.4"),sQuery(id+"F29.wireOp",EDGE,"E533.6"),sQuery(id+"F29.wireOp",EDGE,"E533.8"),sQuery(id+"F29.wireOp",EDGE,"E534.10"),sQuery(id+"F29.wireOp",EDGE,"E534.11"),sQuery(id+"F29.wireOp",EDGE,"E534.12"),sQuery(id+"F29.wireOp",EDGE,"E534.13"),sQuery(id+"F29.wireOp",EDGE,"E534.14"),sQuery(id+"F29.wireOp",EDGE,"E534.15"),sQuery(id+"F29.wireOp",EDGE,"E534.16"),sQuery(id+"F29.wireOp",EDGE,"E534.17"),sQuery(id+"F29.wireOp",EDGE,"E536.trimOffspring"),sQuery(id+"F29.wireOp",EDGE,"E537.trimOffspring"),sQuery(id+"F29.wireOp",EDGE,"E538.MirrorCS"),sQuery(id+"F29.wireOp",EDGE,"E539.MirrorCS"),sQuery(id+"F29.wireOp",EDGE,"E540.MirrorCS"),sQuery(id+"F29.wireOp",EDGE,"E541.MirrorCS"),sQuery(id+"F29.wireOp",EDGE,"E542.MirrorCS"),sQuery(id+"F29.wireOp",EDGE,"E543.MirrorCS"),sQuery(id+"F29.wireOp",EDGE,"E544.MirrorCS"),sQuery(id+"F29.wireOp",EDGE,"E545.trimOffspring"),sQuery(id+"F29.wireOp",EDGE,"E548.0"),sQuery(id+"F29.wireOp",EDGE,"E555.filletArc"),sQuery(id+"F29.wireOp",EDGE,"E556.filletArc"),sQuery(id+"F29.wireOp",EDGE,"E557.filletArc"),sQuery(id+"F29.wireOp",EDGE,"E558.filletArc")])]});
            var Q3;
            Q3=makeQuery(id+"F37.opExtrude","SWEPT_BODY",BODY,{"disambiguationData":[OSD([sQuery(id+"F10.wireOp",EDGE,"E255.16"),sQuery(id+"F10.wireOp",EDGE,"E255.19"),sQuery(id+"F10.wireOp",EDGE,"E255.22"),sQuery(id+"F10.wireOp",EDGE,"E255.23"),sQuery(id+"F10.wireOp",EDGE,"E255.24"),sQuery(id+"F10.wireOp",EDGE,"E255.25"),sQuery(id+"F10.wireOp",EDGE,"E255.26"),sQuery(id+"F10.wireOp",EDGE,"E255.27"),sQuery(id+"F10.wireOp",EDGE,"E255.28"),sQuery(id+"F10.wireOp",EDGE,"E255.30"),sQuery(id+"F10.wireOp",EDGE,"E271.0"),sQuery(id+"F10.wireOp",EDGE,"E277"),sQuery(id+"F10.wireOp",EDGE,"E278"),sQuery(id+"F10.wireOp",EDGE,"E279"),sQuery(id+"F10.wireOp",EDGE,"E280"),sQuery(id+"F10.wireOp",EDGE,"E281.MirrorCS"),sQuery(id+"F10.wireOp",EDGE,"E282.MirrorCS"),sQuery(id+"F10.wireOp",EDGE,"E283.MirrorCS"),sQuery(id+"F10.wireOp",EDGE,"E284.MirrorCS"),sQuery(id+"F10.wireOp",EDGE,"E289.0"),sQuery(id+"F10.wireOp",EDGE,"E289.1"),sQuery(id+"F10.wireOp",EDGE,"E289.2"),sQuery(id+"F10.wireOp",EDGE,"E290.MirrorCS"),sQuery(id+"F10.wireOp",EDGE,"E291.MirrorCS"),sQuery(id+"F10.wireOp",EDGE,"E292.MirrorCS"),sQuery(id+"F10.wireOp",EDGE,"E315.0"),sQuery(id+"F10.wireOp",EDGE,"E321.filletArc"),sQuery(id+"F10.wireOp",EDGE,"E322.filletArc"),sQuery(id+"F10.wireOp",EDGE,"E323.filletArc"),sQuery(id+"F10.wireOp",EDGE,"E324.filletArc")])]});
            var Q4;
            Q4=makeQuery(id+"F37.opExtrude","SWEPT_BODY",BODY,{"disambiguationData":[OSD([sQuery(id+"F10.wireOp",EDGE,"E255.0"),sQuery(id+"F10.wireOp",EDGE,"E255.2"),sQuery(id+"F10.wireOp",EDGE,"E255.5"),sQuery(id+"F10.wireOp",EDGE,"E255.6"),sQuery(id+"F10.wireOp",EDGE,"E255.7"),sQuery(id+"F10.wireOp",EDGE,"E255.9"),sQuery(id+"F10.wireOp",EDGE,"E255.10"),sQuery(id+"F10.wireOp",EDGE,"E255.11"),sQuery(id+"F10.wireOp",EDGE,"E255.12"),sQuery(id+"F10.wireOp",EDGE,"E255.14"),sQuery(id+"F10.wireOp",EDGE,"E257.0"),sQuery(id+"F10.wireOp",EDGE,"E261"),sQuery(id+"F10.wireOp",EDGE,"E262"),sQuery(id+"F10.wireOp",EDGE,"E263"),sQuery(id+"F10.wireOp",EDGE,"E264"),sQuery(id+"F10.wireOp",EDGE,"E267.MirrorCS"),sQuery(id+"F10.wireOp",EDGE,"E268.MirrorCS"),sQuery(id+"F10.wireOp",EDGE,"E269.MirrorCS"),sQuery(id+"F10.wireOp",EDGE,"E270.MirrorCS"),sQuery(id+"F10.wireOp",EDGE,"E285.0"),sQuery(id+"F10.wireOp",EDGE,"E285.1"),sQuery(id+"F10.wireOp",EDGE,"E285.2"),sQuery(id+"F10.wireOp",EDGE,"E286.MirrorCS"),sQuery(id+"F10.wireOp",EDGE,"E287.MirrorCS"),sQuery(id+"F10.wireOp",EDGE,"E288.MirrorCS"),sQuery(id+"F10.wireOp",EDGE,"E314.0"),sQuery(id+"F10.wireOp",EDGE,"E317.filletArc"),sQuery(id+"F10.wireOp",EDGE,"E318.filletArc"),sQuery(id+"F10.wireOp",EDGE,"E319.filletArc"),sQuery(id+"F10.wireOp",EDGE,"E320.filletArc")])]});
            var Q5;
            Q5=makeQuery(id+"F37.opExtrude","SWEPT_BODY",BODY,{"disambiguationData":[OSD([sQuery(id+"F29.wireOp",EDGE,"E519.0"),sQuery(id+"F29.wireOp",EDGE,"E519.1"),sQuery(id+"F29.wireOp",EDGE,"E519.2"),sQuery(id+"F29.wireOp",EDGE,"E519.3"),sQuery(id+"F29.wireOp",EDGE,"E519.4"),sQuery(id+"F29.wireOp",EDGE,"E519.5"),sQuery(id+"F29.wireOp",EDGE,"E519.6"),sQuery(id+"F29.wireOp",EDGE,"E519.7"),sQuery(id+"F29.wireOp",EDGE,"E520.0"),sQuery(id+"F29.wireOp",EDGE,"E520.1"),sQuery(id+"F29.wireOp",EDGE,"E520.2"),sQuery(id+"F29.wireOp",EDGE,"E520.3"),sQuery(id+"F29.wireOp",EDGE,"E520.4"),sQuery(id+"F29.wireOp",EDGE,"E520.6"),sQuery(id+"F29.wireOp",EDGE,"E520.7"),sQuery(id+"F29.wireOp",EDGE,"E521.trimOffspring"),sQuery(id+"F29.wireOp",EDGE,"E522.trimOffspring"),sQuery(id+"F29.wireOp",EDGE,"E524.MirrorCS"),sQuery(id+"F29.wireOp",EDGE,"E525.MirrorCS"),sQuery(id+"F29.wireOp",EDGE,"E526.MirrorCS"),sQuery(id+"F29.wireOp",EDGE,"E527.MirrorCS"),sQuery(id+"F29.wireOp",EDGE,"E528.MirrorCS"),sQuery(id+"F29.wireOp",EDGE,"E529.MirrorCS"),sQuery(id+"F29.wireOp",EDGE,"E530.MirrorCS"),sQuery(id+"F29.wireOp",EDGE,"E531.trimOffspring"),sQuery(id+"F29.wireOp",EDGE,"E549.0"),sQuery(id+"F29.wireOp",EDGE,"E559.filletArc"),sQuery(id+"F29.wireOp",EDGE,"E560.filletArc"),sQuery(id+"F29.wireOp",EDGE,"E561.filletArc"),sQuery(id+"F29.wireOp",EDGE,"E562.filletArc")])]});
            var Q6;
            Q6=makeQuery(id+"F42.opExtrude","SWEPT_BODY",BODY,{"disambiguationData":[OSD([sQuery(id+"F11.wireOp",EDGE,"E339.MirrorC"),sQuery(id+"F11.wireOp",EDGE,"E340.MirrorC"),sQuery(id+"F11.wireOp",EDGE,"E341.bottom"),sQuery(id+"F11.wireOp",EDGE,"E341.top"),sQuery(id+"F11.wireOp",EDGE,"E346.MirrorCS"),sQuery(id+"F11.wireOp",EDGE,"E348.MirrorC"),sQuery(id+"F11.wireOp",EDGE,"E350.MirrorCS")])]});
            var Q7;
            Q7=makeQuery(id+"F45.opExtrude","SWEPT_BODY",BODY,{"disambiguationData":[OSD([sQuery(id+"F11.wireOp",EDGE,"E341.bottom"),sQuery(id+"F11.wireOp",EDGE,"E341.top"),sQuery(id+"F11.wireOp",EDGE,"E344.MirrorCS"),sQuery(id+"F11.wireOp",EDGE,"E350.MirrorCS")])]});
            var Q8;
            Q8=makeQuery(id+"F42.opExtrude","SWEPT_BODY",BODY,{"disambiguationData":[OSD([sQuery(id+"F11.wireOp",EDGE,"E336"),sQuery(id+"F11.wireOp",EDGE,"E338"),sQuery(id+"F11.wireOp",EDGE,"E341.bottom"),sQuery(id+"F11.wireOp",EDGE,"E341.top"),sQuery(id+"F11.wireOp",EDGE,"E344.MirrorCS"),sQuery(id+"F11.wireOp",EDGE,"E345"),sQuery(id+"F11.wireOp",EDGE,"E347")])]});
            var Q9;
            Q9=makeQuery(id+"F41.opExtrude","SWEPT_BODY",BODY,{"disambiguationData":[OSD([sQuery(id+"F32.wireOp",EDGE,"E569.0"),sQuery(id+"F32.wireOp",EDGE,"E569.1"),sQuery(id+"F32.wireOp",EDGE,"E569.2"),sQuery(id+"F32.wireOp",EDGE,"E569.3"),sQuery(id+"F32.wireOp",EDGE,"E569.4"),sQuery(id+"F32.wireOp",EDGE,"E569.5"),sQuery(id+"F32.wireOp",EDGE,"E569.6"),sQuery(id+"F32.wireOp",EDGE,"E570.0")])]});
            var Q10;
            Q10=makeQuery(id+"F40.opExtrude","SWEPT_BODY",BODY,{"disambiguationData":[OSD([sQuery(id+"F9.wireOp",EDGE,"E106"),sQuery(id+"F9.wireOp",EDGE,"E120"),sQuery(id+"F9.wireOp",EDGE,"E121"),sQuery(id+"F9.wireOp",EDGE,"E122")])]});
            var Q11;
            Q11=makeQuery(id+"F41.opExtrude","SWEPT_BODY",BODY,{"disambiguationData":[OSD([sQuery(id+"F32.wireOp",EDGE,"E567.0"),sQuery(id+"F32.wireOp",EDGE,"E567.1"),sQuery(id+"F32.wireOp",EDGE,"E567.2"),sQuery(id+"F32.wireOp",EDGE,"E567.4"),sQuery(id+"F32.wireOp",EDGE,"E567.5"),sQuery(id+"F32.wireOp",EDGE,"E567.6"),sQuery(id+"F32.wireOp",EDGE,"E567.7"),sQuery(id+"F32.wireOp",EDGE,"E568.trimOffspring")])]});
            var Q12;
            Q12=makeQuery(id+"F37.opExtrude","SWEPT_BODY",BODY,{"disambiguationData":[OSD([sQuery(id+"F31.wireOp",EDGE,"E565.0"),sQuery(id+"F31.wireOp",EDGE,"E565.6"),sQuery(id+"F31.wireOp",EDGE,"E565.7"),sQuery(id+"F31.wireOp",EDGE,"E566.0"),sQuery(id+"F31.wireOp",EDGE,"E566.1"),sQuery(id+"F31.wireOp",EDGE,"E566.2"),sQuery(id+"F31.wireOp",EDGE,"E566.3"),sQuery(id+"F31.wireOp",EDGE,"E566.4")])]});
            var Q13;
            Q13=qCreatedBy(id+"F34.planeOp",FACE);
            mirror(context, id + "F49", {"entities" : qUnion([Q0, Q1, Q2, Q3, Q4, Q5, Q6, Q7, Q8, Q9, Q10, Q11, Q12]), "mirrorPlane" : qUnion([Q13])});
        }
        {
            var Q0;
            Q0=makeQuery(id+"F40.opExtrude","SWEPT_BODY",BODY,{"disambiguationData":[OSD([sQuery(id+"F9.wireOp",EDGE,"E176"),sQuery(id+"F9.wireOp",EDGE,"E178"),sQuery(id+"F9.wireOp",EDGE,"E180"),sQuery(id+"F9.wireOp",EDGE,"E204"),sQuery(id+"F9.wireOp",EDGE,"E205"),sQuery(id+"F9.wireOp",EDGE,"E218")])]});
            var Q1;
            Q1=makeQuery(id+"F40.opExtrude","SWEPT_BODY",BODY,{"disambiguationData":[OSD([sQuery(id+"F9.wireOp",EDGE,"E138"),sQuery(id+"F9.wireOp",EDGE,"E139"),sQuery(id+"F9.wireOp",EDGE,"E140"),sQuery(id+"F9.wireOp",EDGE,"E162.MirrorCS")])]});
            var Q2;
            Q2=makeQuery(id+"F38.opExtrude","SWEPT_BODY",BODY,{"disambiguationData":[OSD([sQuery(id+"F26.wireOp",EDGE,"E485"),sQuery(id+"F26.wireOp",EDGE,"E486"),sQuery(id+"F26.wireOp",EDGE,"E487"),sQuery(id+"F26.wireOp",EDGE,"E488"),sQuery(id+"F26.wireOp",EDGE,"E489"),sQuery(id+"F26.wireOp",EDGE,"E490"),sQuery(id+"F26.wireOp",EDGE,"E491"),sQuery(id+"F26.wireOp",EDGE,"E492.MirrorCS"),sQuery(id+"F26.wireOp",EDGE,"E493.MirrorCS"),sQuery(id+"F26.wireOp",EDGE,"E494.MirrorCS"),sQuery(id+"F26.wireOp",EDGE,"E495.MirrorCS"),sQuery(id+"F26.wireOp",EDGE,"E496.MirrorCS"),sQuery(id+"F26.wireOp",EDGE,"E497.MirrorCS"),sQuery(id+"F26.wireOp",EDGE,"E498.MirrorCS"),sQuery(id+"F26.wireOp",EDGE,"E499"),sQuery(id+"F26.wireOp",EDGE,"E500")])]});
            var Q3;
            Q3=makeQuery(id+"F37.opExtrude","SWEPT_BODY",BODY,{"disambiguationData":[OSD([sQuery(id+"F29.wireOp",EDGE,"E533.9"),sQuery(id+"F29.wireOp",EDGE,"E533.10"),sQuery(id+"F29.wireOp",EDGE,"E533.11"),sQuery(id+"F29.wireOp",EDGE,"E533.12"),sQuery(id+"F29.wireOp",EDGE,"E533.13"),sQuery(id+"F29.wireOp",EDGE,"E533.14"),sQuery(id+"F29.wireOp",EDGE,"E533.15"),sQuery(id+"F29.wireOp",EDGE,"E533.16"),sQuery(id+"F29.wireOp",EDGE,"E533.17"),sQuery(id+"F29.wireOp",EDGE,"E533.18"),sQuery(id+"F29.wireOp",EDGE,"E533.19"),sQuery(id+"F29.wireOp",EDGE,"E533.20"),sQuery(id+"F29.wireOp",EDGE,"E533.21"),sQuery(id+"F29.wireOp",EDGE,"E534.1"),sQuery(id+"F29.wireOp",EDGE,"E534.3"),sQuery(id+"F29.wireOp",EDGE,"E534.4"),sQuery(id+"F29.wireOp",EDGE,"E534.5"),sQuery(id+"F29.wireOp",EDGE,"E534.6"),sQuery(id+"F29.wireOp",EDGE,"E534.7"),sQuery(id+"F29.wireOp",EDGE,"E534.8"),sQuery(id+"F29.wireOp",EDGE,"E534.9"),sQuery(id+"F29.wireOp",EDGE,"E546.trimOffspring"),sQuery(id+"F29.wireOp",EDGE,"E550.0"),sQuery(id+"F29.wireOp",EDGE,"E550.1"),sQuery(id+"F29.wireOp",EDGE,"E551.0"),sQuery(id+"F29.wireOp",EDGE,"E551.1"),sQuery(id+"F29.wireOp",EDGE,"E551.2"),sQuery(id+"F29.wireOp",EDGE,"E551.3"),sQuery(id+"F29.wireOp",EDGE,"E552.0"),sQuery(id+"F29.wireOp",EDGE,"E552.1"),sQuery(id+"F29.wireOp",EDGE,"E552.2"),sQuery(id+"F29.wireOp",EDGE,"E552.4"),sQuery(id+"F29.wireOp",EDGE,"E553.filletArc"),sQuery(id+"F29.wireOp",EDGE,"E554.filletArc"),sQuery(id+"F29.wireOp",EDGE,"E563.0"),sQuery(id+"F29.wireOp",EDGE,"E564.0")])]});
            var Q4;
            Q4=makeQuery(id+"F38.opExtrude","SWEPT_BODY",BODY,{"disambiguationData":[OSD([sQuery(id+"F25.wireOp",EDGE,"E464"),sQuery(id+"F25.wireOp",EDGE,"E465"),sQuery(id+"F25.wireOp",EDGE,"E466"),sQuery(id+"F25.wireOp",EDGE,"E467"),sQuery(id+"F25.wireOp",EDGE,"E469.MirrorCS"),sQuery(id+"F25.wireOp",EDGE,"E471.MirrorCS"),sQuery(id+"F25.wireOp",EDGE,"E472.MirrorCS"),sQuery(id+"F25.wireOp",EDGE,"E473.MirrorCS"),sQuery(id+"F25.wireOp",EDGE,"E474"),sQuery(id+"F25.wireOp",EDGE,"E475"),sQuery(id+"F25.wireOp",EDGE,"E476"),sQuery(id+"F25.wireOp",EDGE,"E477.trimOffspring"),sQuery(id+"F25.wireOp",EDGE,"E478.MirrorCS"),sQuery(id+"F25.wireOp",EDGE,"E479.MirrorCS"),sQuery(id+"F25.wireOp",EDGE,"E470.MirrorCS"),sQuery(id+"F25.wireOp",EDGE,"E480.trimOffspring")])]});
            var Q5;
            Q5=makeQuery(id+"F48.opPattern","COPY",BODY,{"derivedFrom":makeQuery(id+"F38.opExtrude","SWEPT_BODY",BODY,{"disambiguationData":[OSD([sQuery(id+"F19.wireOp",EDGE,"E413"),sQuery(id+"F19.wireOp",EDGE,"E414"),sQuery(id+"F19.wireOp",EDGE,"E415.MirrorCS"),sQuery(id+"F19.wireOp",EDGE,"E416.top"),sQuery(id+"F19.wireOp",EDGE,"E416.left"),sQuery(id+"F19.wireOp",EDGE,"E416.right"),sQuery(id+"F19.wireOp",EDGE,"E418"),sQuery(id+"F19.wireOp",EDGE,"E419"),sQuery(id+"F19.wireOp",EDGE,"E420.MirrorCS"),sQuery(id+"F19.wireOp",EDGE,"E421.MirrorCS"),sQuery(id+"F19.wireOp",EDGE,"E422.MirrorCS"),sQuery(id+"F19.wireOp",EDGE,"E423.MirrorCS"),sQuery(id+"F19.wireOp",EDGE,"E424.MirrorCS"),sQuery(id+"F19.wireOp",EDGE,"E425.MirrorCS"),sQuery(id+"F19.wireOp",EDGE,"E426"),sQuery(id+"F19.wireOp",EDGE,"E427")])]}),"instanceName":"1"});
            var Q6;
            Q6=makeQuery(id+"F48.opPattern","COPY",BODY,{"derivedFrom":makeQuery(id+"F38.opExtrude","SWEPT_BODY",BODY,{"disambiguationData":[OSD([sQuery(id+"F17.wireOp",EDGE,"E395"),sQuery(id+"F17.wireOp",EDGE,"E396"),sQuery(id+"F17.wireOp",EDGE,"E397"),sQuery(id+"F17.wireOp",EDGE,"E398.MirrorCS"),sQuery(id+"F17.wireOp",EDGE,"E399.MirrorCS"),sQuery(id+"F17.wireOp",EDGE,"E400.MirrorCS"),sQuery(id+"F17.wireOp",EDGE,"E401"),sQuery(id+"F17.wireOp",EDGE,"E402"),sQuery(id+"F17.wireOp",EDGE,"E403.bottom"),sQuery(id+"F17.wireOp",EDGE,"E403.left"),sQuery(id+"F17.wireOp",EDGE,"E403.right"),sQuery(id+"F17.wireOp",EDGE,"E404.trimOffspring"),sQuery(id+"F17.wireOp",EDGE,"E405.MirrorCS"),sQuery(id+"F17.wireOp",EDGE,"E406.MirrorCS"),sQuery(id+"F17.wireOp",EDGE,"E407.MirrorCS"),sQuery(id+"F17.wireOp",EDGE,"E408.trimOffspring")])]}),"instanceName":"1"});
            var Q7;
            Q7=makeQuery(id+"F38.opExtrude","SWEPT_BODY",BODY,{"disambiguationData":[OSD([sQuery(id+"F19.wireOp",EDGE,"E413"),sQuery(id+"F19.wireOp",EDGE,"E414"),sQuery(id+"F19.wireOp",EDGE,"E415.MirrorCS"),sQuery(id+"F19.wireOp",EDGE,"E416.top"),sQuery(id+"F19.wireOp",EDGE,"E416.left"),sQuery(id+"F19.wireOp",EDGE,"E416.right"),sQuery(id+"F19.wireOp",EDGE,"E418"),sQuery(id+"F19.wireOp",EDGE,"E419"),sQuery(id+"F19.wireOp",EDGE,"E420.MirrorCS"),sQuery(id+"F19.wireOp",EDGE,"E421.MirrorCS"),sQuery(id+"F19.wireOp",EDGE,"E422.MirrorCS"),sQuery(id+"F19.wireOp",EDGE,"E423.MirrorCS"),sQuery(id+"F19.wireOp",EDGE,"E424.MirrorCS"),sQuery(id+"F19.wireOp",EDGE,"E425.MirrorCS"),sQuery(id+"F19.wireOp",EDGE,"E426"),sQuery(id+"F19.wireOp",EDGE,"E427")])]});
            var Q8;
            Q8=makeQuery(id+"F47.opPattern","COPY",BODY,{"derivedFrom":makeQuery(id+"F38.opExtrude","SWEPT_BODY",BODY,{"disambiguationData":[OSD([sQuery(id+"F15.wireOp",EDGE,"E373"),sQuery(id+"F15.wireOp",EDGE,"E374"),sQuery(id+"F15.wireOp",EDGE,"E377.MirrorCS"),sQuery(id+"F15.wireOp",EDGE,"E378"),sQuery(id+"F15.wireOp",EDGE,"E379.top"),sQuery(id+"F15.wireOp",EDGE,"E381"),sQuery(id+"F15.wireOp",EDGE,"E382"),sQuery(id+"F15.wireOp",EDGE,"E383"),sQuery(id+"F15.wireOp",EDGE,"E384"),sQuery(id+"F15.wireOp",EDGE,"E385.trimOffspring"),sQuery(id+"F15.wireOp",EDGE,"E386.MirrorCS"),sQuery(id+"F15.wireOp",EDGE,"E387.MirrorCS"),sQuery(id+"F15.wireOp",EDGE,"E388.MirrorCS"),sQuery(id+"F15.wireOp",EDGE,"E389.MirrorCS"),sQuery(id+"F15.wireOp",EDGE,"E390.MirrorCS"),sQuery(id+"F15.wireOp",EDGE,"E391.trimOffspring")])]}),"instanceName":"1"});
            var Q9;
            Q9=makeQuery(id+"F47.opPattern","COPY",BODY,{"derivedFrom":makeQuery(id+"F38.opExtrude","SWEPT_BODY",BODY,{"disambiguationData":[OSD([sQuery(id+"F13.wireOp",EDGE,"E354"),sQuery(id+"F13.wireOp",EDGE,"E355"),sQuery(id+"F13.wireOp",EDGE,"E356"),sQuery(id+"F13.wireOp",EDGE,"E357"),sQuery(id+"F13.wireOp",EDGE,"E359"),sQuery(id+"F13.wireOp",EDGE,"E361.MirrorCS"),sQuery(id+"F13.wireOp",EDGE,"E362.MirrorCS"),sQuery(id+"F13.wireOp",EDGE,"E363.MirrorCS"),sQuery(id+"F13.wireOp",EDGE,"E364"),sQuery(id+"F13.wireOp",EDGE,"E365"),sQuery(id+"F13.wireOp",EDGE,"E366.MirrorCS"),sQuery(id+"F13.wireOp",EDGE,"E360.MirrorCS"),sQuery(id+"F13.wireOp",EDGE,"E367.MirrorCS"),sQuery(id+"F13.wireOp",EDGE,"E368.MirrorCS"),sQuery(id+"F13.wireOp",EDGE,"E369"),sQuery(id+"F13.wireOp",EDGE,"E370")])]}),"instanceName":"1"});
            var Q10;
            Q10=makeQuery(id+"F38.opExtrude","SWEPT_BODY",BODY,{"disambiguationData":[OSD([sQuery(id+"F13.wireOp",EDGE,"E354"),sQuery(id+"F13.wireOp",EDGE,"E355"),sQuery(id+"F13.wireOp",EDGE,"E356"),sQuery(id+"F13.wireOp",EDGE,"E357"),sQuery(id+"F13.wireOp",EDGE,"E359"),sQuery(id+"F13.wireOp",EDGE,"E361.MirrorCS"),sQuery(id+"F13.wireOp",EDGE,"E362.MirrorCS"),sQuery(id+"F13.wireOp",EDGE,"E363.MirrorCS"),sQuery(id+"F13.wireOp",EDGE,"E364"),sQuery(id+"F13.wireOp",EDGE,"E365"),sQuery(id+"F13.wireOp",EDGE,"E366.MirrorCS"),sQuery(id+"F13.wireOp",EDGE,"E360.MirrorCS"),sQuery(id+"F13.wireOp",EDGE,"E367.MirrorCS"),sQuery(id+"F13.wireOp",EDGE,"E368.MirrorCS"),sQuery(id+"F13.wireOp",EDGE,"E369"),sQuery(id+"F13.wireOp",EDGE,"E370")])]});
            var Q11;
            Q11=makeQuery(id+"F38.opExtrude","SWEPT_BODY",BODY,{"disambiguationData":[OSD([sQuery(id+"F15.wireOp",EDGE,"E373"),sQuery(id+"F15.wireOp",EDGE,"E374"),sQuery(id+"F15.wireOp",EDGE,"E377.MirrorCS"),sQuery(id+"F15.wireOp",EDGE,"E378"),sQuery(id+"F15.wireOp",EDGE,"E379.top"),sQuery(id+"F15.wireOp",EDGE,"E381"),sQuery(id+"F15.wireOp",EDGE,"E382"),sQuery(id+"F15.wireOp",EDGE,"E383"),sQuery(id+"F15.wireOp",EDGE,"E384"),sQuery(id+"F15.wireOp",EDGE,"E385.trimOffspring"),sQuery(id+"F15.wireOp",EDGE,"E386.MirrorCS"),sQuery(id+"F15.wireOp",EDGE,"E387.MirrorCS"),sQuery(id+"F15.wireOp",EDGE,"E388.MirrorCS"),sQuery(id+"F15.wireOp",EDGE,"E389.MirrorCS"),sQuery(id+"F15.wireOp",EDGE,"E390.MirrorCS"),sQuery(id+"F15.wireOp",EDGE,"E391.trimOffspring")])]});
            var Q12;
            Q12=makeQuery(id+"F40.opExtrude","SWEPT_BODY",BODY,{"disambiguationData":[OSD([sQuery(id+"F9.wireOp",EDGE,"E106"),sQuery(id+"F9.wireOp",EDGE,"E120"),sQuery(id+"F9.wireOp",EDGE,"E121"),sQuery(id+"F9.wireOp",EDGE,"E122")])]});
            var Q13;
            Q13=makeQuery(id+"F41.opExtrude","SWEPT_BODY",BODY,{"disambiguationData":[OSD([sQuery(id+"F32.wireOp",EDGE,"E569.0"),sQuery(id+"F32.wireOp",EDGE,"E569.1"),sQuery(id+"F32.wireOp",EDGE,"E569.2"),sQuery(id+"F32.wireOp",EDGE,"E569.3"),sQuery(id+"F32.wireOp",EDGE,"E569.4"),sQuery(id+"F32.wireOp",EDGE,"E569.5"),sQuery(id+"F32.wireOp",EDGE,"E569.6"),sQuery(id+"F32.wireOp",EDGE,"E570.0")])]});
            var Q14;
            Q14=makeQuery(id+"F40.opExtrude","SWEPT_BODY",BODY,{"disambiguationData":[OSD([sQuery(id+"F9.wireOp",EDGE,"E113"),sQuery(id+"F9.wireOp",EDGE,"E129.left"),sQuery(id+"F9.wireOp",EDGE,"E129.right"),sQuery(id+"F9.wireOp",EDGE,"E220"),sQuery(id+"F9.wireOp",EDGE,"E221")])]});
            var Q15;
            Q15=makeQuery(id+"F38.opExtrude","SWEPT_BODY",BODY,{"disambiguationData":[OSD([sQuery(id+"F17.wireOp",EDGE,"E395"),sQuery(id+"F17.wireOp",EDGE,"E396"),sQuery(id+"F17.wireOp",EDGE,"E397"),sQuery(id+"F17.wireOp",EDGE,"E398.MirrorCS"),sQuery(id+"F17.wireOp",EDGE,"E399.MirrorCS"),sQuery(id+"F17.wireOp",EDGE,"E400.MirrorCS"),sQuery(id+"F17.wireOp",EDGE,"E401"),sQuery(id+"F17.wireOp",EDGE,"E402"),sQuery(id+"F17.wireOp",EDGE,"E403.bottom"),sQuery(id+"F17.wireOp",EDGE,"E403.left"),sQuery(id+"F17.wireOp",EDGE,"E403.right"),sQuery(id+"F17.wireOp",EDGE,"E404.trimOffspring"),sQuery(id+"F17.wireOp",EDGE,"E405.MirrorCS"),sQuery(id+"F17.wireOp",EDGE,"E406.MirrorCS"),sQuery(id+"F17.wireOp",EDGE,"E407.MirrorCS"),sQuery(id+"F17.wireOp",EDGE,"E408.trimOffspring")])]});
            var Q16;
            Q16=makeQuery(id+"F40.opExtrude","SWEPT_BODY",BODY,{"disambiguationData":[OSD([sQuery(id+"F9.wireOp",EDGE,"E147"),sQuery(id+"F9.wireOp",EDGE,"E155.left"),sQuery(id+"F9.wireOp",EDGE,"E155.right"),sQuery(id+"F9.wireOp",EDGE,"E222"),sQuery(id+"F9.wireOp",EDGE,"7zd2PVgX-ojsz-AN5h-69Uh-4DySPVRgbPLi")])]});
            var Q17;
            Q17=makeQuery(id+"F38.opExtrude","SWEPT_BODY",BODY,{"disambiguationData":[OSD([sQuery(id+"F24.wireOp",EDGE,"E430"),sQuery(id+"F24.wireOp",EDGE,"E431"),sQuery(id+"F24.wireOp",EDGE,"E432"),sQuery(id+"F24.wireOp",EDGE,"E433"),sQuery(id+"F24.wireOp",EDGE,"E434"),sQuery(id+"F24.wireOp",EDGE,"E435"),sQuery(id+"F24.wireOp",EDGE,"E436"),sQuery(id+"F24.wireOp",EDGE,"E438.MirrorCS"),sQuery(id+"F24.wireOp",EDGE,"E439.MirrorCS"),sQuery(id+"F24.wireOp",EDGE,"E440.MirrorCS"),sQuery(id+"F24.wireOp",EDGE,"E441.MirrorCS"),sQuery(id+"F24.wireOp",EDGE,"E442.MirrorCS"),sQuery(id+"F24.wireOp",EDGE,"E443.MirrorCS"),sQuery(id+"F24.wireOp",EDGE,"E444.MirrorCS"),sQuery(id+"F24.wireOp",EDGE,"E445"),sQuery(id+"F24.wireOp",EDGE,"E446"),sQuery(id+"F24.wireOp",EDGE,"E448"),sQuery(id+"F24.wireOp",EDGE,"E449"),sQuery(id+"F24.wireOp",EDGE,"E450"),sQuery(id+"F24.wireOp",EDGE,"E451.trimOffspring"),sQuery(id+"F24.wireOp",EDGE,"E452"),sQuery(id+"F24.wireOp",EDGE,"E453"),sQuery(id+"F24.wireOp",EDGE,"E454"),sQuery(id+"F24.wireOp",EDGE,"E455.trimOffspring"),sQuery(id+"F24.wireOp",EDGE,"E456.MirrorCS"),sQuery(id+"F24.wireOp",EDGE,"E457.MirrorCS"),sQuery(id+"F24.wireOp",EDGE,"E458.MirrorCS"),sQuery(id+"F24.wireOp",EDGE,"E459.trimOffspring")])]});
            var Q18;
            Q18=makeQuery(id+"F44.opExtrude","SWEPT_BODY",BODY,{"disambiguationData":[OSD([sQuery(id+"F33.wireOp",EDGE,"E572"),sQuery(id+"F33.wireOp",EDGE,"E573"),sQuery(id+"F33.wireOp",EDGE,"E574"),sQuery(id+"F33.wireOp",EDGE,"E575"),sQuery(id+"F33.wireOp",EDGE,"E576"),sQuery(id+"F33.wireOp",EDGE,"E585"),sQuery(id+"F33.wireOp",EDGE,"E586.1"),sQuery(id+"F33.wireOp",EDGE,"E587"),sQuery(id+"F33.wireOp",EDGE,"E588"),sQuery(id+"F33.wireOp",EDGE,"E589"),sQuery(id+"F33.wireOp",EDGE,"E590"),sQuery(id+"F33.wireOp",EDGE,"E592.MirrorCS"),sQuery(id+"F33.wireOp",EDGE,"E593.MirrorCS"),sQuery(id+"F33.wireOp",EDGE,"E594.MirrorCS"),sQuery(id+"F33.wireOp",EDGE,"E595.MirrorCS"),sQuery(id+"F33.wireOp",EDGE,"E600.MirrorCS"),sQuery(id+"F33.wireOp",EDGE,"E601.MirrorCS"),sQuery(id+"F33.wireOp",EDGE,"E602.MirrorCS"),sQuery(id+"F33.wireOp",EDGE,"E603.MirrorCS")])]});
            var Q19;
            Q19=makeQuery(id+"F44.opExtrude","SWEPT_BODY",BODY,{"disambiguationData":[OSD([sQuery(id+"F33.wireOp",EDGE,"E605.1.0.0"),sQuery(id+"F33.wireOp",EDGE,"E605.1.0.1"),sQuery(id+"F33.wireOp",EDGE,"E605.1.0.2"),sQuery(id+"F33.wireOp",EDGE,"E605.1.0.3"),sQuery(id+"F33.wireOp",EDGE,"E605.1.0.4"),sQuery(id+"F33.wireOp",EDGE,"E605.1.0.5"),sQuery(id+"F33.wireOp",EDGE,"E605.1.0.6"),sQuery(id+"F33.wireOp",EDGE,"E605.1.0.7"),sQuery(id+"F33.wireOp",EDGE,"E605.1.0.8"),sQuery(id+"F33.wireOp",EDGE,"E605.1.0.9"),sQuery(id+"F33.wireOp",EDGE,"E605.1.0.10"),sQuery(id+"F33.wireOp",EDGE,"E605.1.0.11"),sQuery(id+"F33.wireOp",EDGE,"E605.1.0.12"),sQuery(id+"F33.wireOp",EDGE,"E605.1.0.13"),sQuery(id+"F33.wireOp",EDGE,"E605.1.0.14"),sQuery(id+"F33.wireOp",EDGE,"E605.1.0.15"),sQuery(id+"F33.wireOp",EDGE,"E605.1.0.16"),sQuery(id+"F33.wireOp",EDGE,"E605.1.0.17"),sQuery(id+"F33.wireOp",EDGE,"E605.1.0.18")])]});
            var Q20;
            Q20=qCreatedBy(id+"F36.planeOp",FACE);
            mirror(context, id + "F50", {"entities" : qUnion([Q0, Q1, Q2, Q3, Q4, Q5, Q6, Q7, Q8, Q9, Q10, Q11, Q12, Q13, Q14, Q15, Q16, Q17, Q18, Q19]), "mirrorPlane" : qUnion([Q20])});
        }
    });
